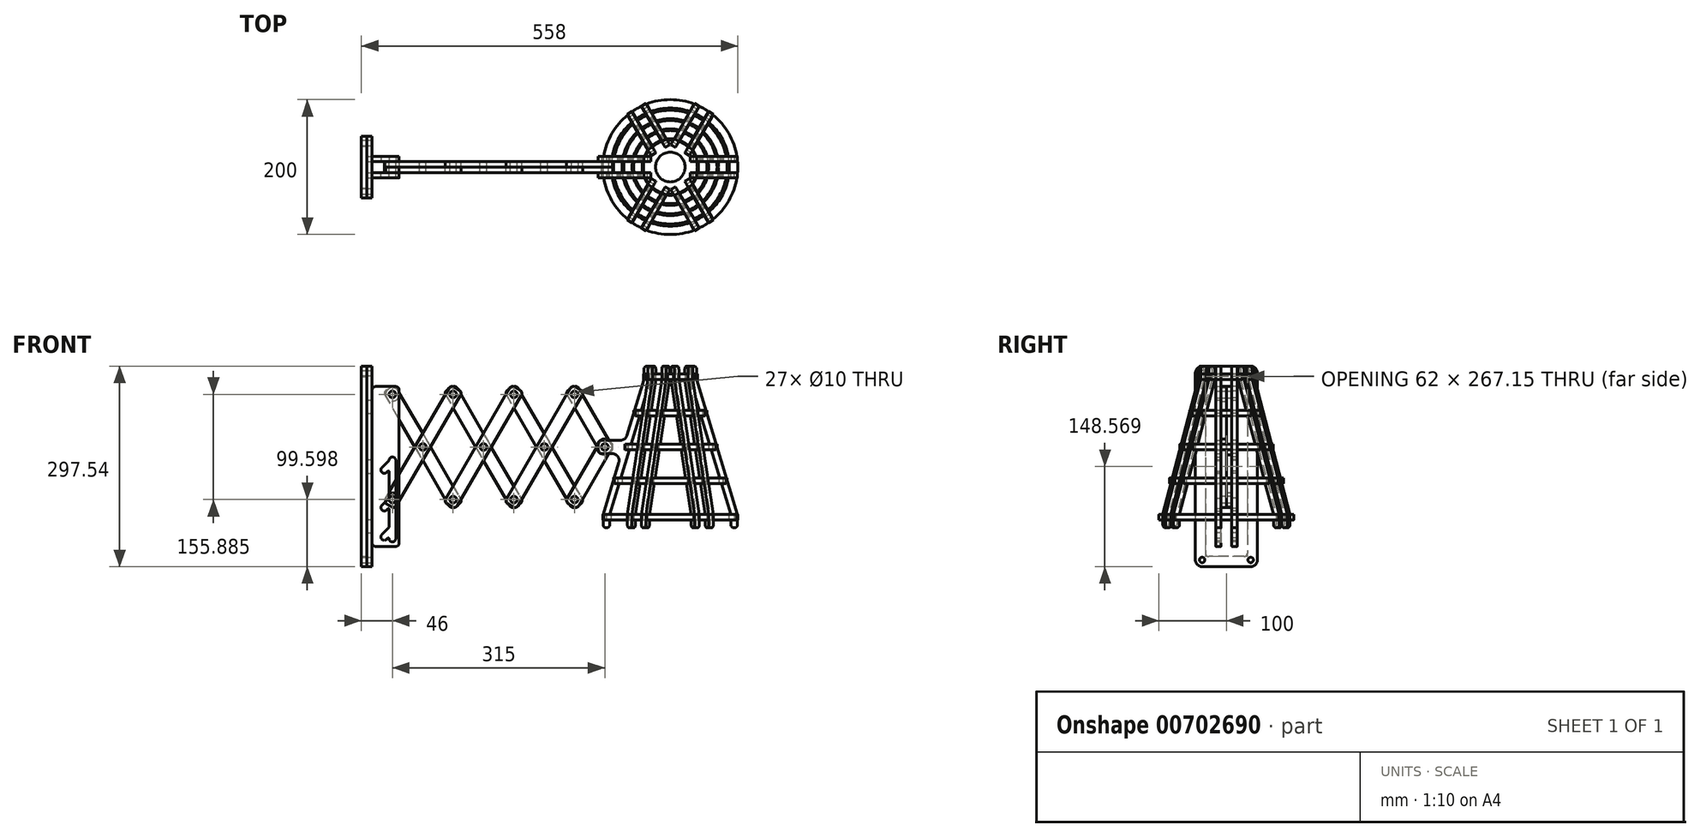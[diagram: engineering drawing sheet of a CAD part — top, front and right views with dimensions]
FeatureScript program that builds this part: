
annotation { "Feature Type Name" : "Feature", "Feature Type Description" : "" }
export const myFeature = defineFeature(function(context is Context, id is Id, definition is map)
    precondition{}
    {
        {
            var Q0;
            Q0=qCreatedBy(makeId("Front.planeOp"),FACE);
            var sketch = newSketch(context, id + "F0", { "sketchPlane" : qUnion([Q0])});
            skLineSegment(sketch, "E0.bottom", {"start": v(54.33, 84.1) * mm, "end": v(45.67, 89.1) * mm});
            skLineSegment(sketch, "E0.top", {"start": v(-45.67, -89.1) * mm, "end": v(-54.33, -84.1) * mm});
            skLineSegment(sketch, "E0.left", {"start": v(56.16, 77.27) * mm, "end": v(-38.84, -87.27) * mm});
            skLineSegment(sketch, "E0.right", {"start": v(38.84, 87.27) * mm, "end": v(-56.16, -77.27) * mm});
            skPoint(sketch, "E0.middle", {"position": v(0, 0) * mm});
            skLineSegment(sketch, "E1", {"start": v(0, 185.82) * mm, "end": v(0, -203.94) * mm, "construction": true});
            skLineSegment(sketch, "E2", {"start": v(-279.88, 0) * mm, "end": v(337.24, 0) * mm, "construction": true});
            skCircle(sketch, "E3", {"center": v(0, 0) * mm, "radius": 5 * mm});
            skCircle(sketch, "E4", {"center": v(45, 77.94) * mm, "radius": 5 * mm});
            skCircle(sketch, "E5.MirrorC", {"center": v(-45, -77.94) * mm, "radius": 5 * mm});
            skPoint(sketch, "E6.visualSharp", {"position": v(41.34, 91.6) * mm});
            skArc(sketch, "E6.filletArc", {"start": v(45.67, 89.1) * mm, "mid": v(41.88, 89.6) * mm, "end": v(38.84, 87.27) * mm});
            skPoint(sketch, "E7.visualSharp", {"position": v(58.66, 81.6) * mm});
            skArc(sketch, "E7.filletArc", {"start": v(56.16, 77.27) * mm, "mid": v(56.66, 81.07) * mm, "end": v(54.33, 84.1) * mm});
            skPoint(sketch, "E8.visualSharp", {"position": v(-41.34, -91.6) * mm});
            skArc(sketch, "E8.filletArc", {"start": v(-45.67, -89.1) * mm, "mid": v(-41.88, -89.6) * mm, "end": v(-38.84, -87.27) * mm});
            skPoint(sketch, "E9.visualSharp", {"position": v(-58.66, -81.6) * mm});
            skArc(sketch, "E9.filletArc", {"start": v(-56.16, -77.27) * mm, "mid": v(-56.66, -81.07) * mm, "end": v(-54.33, -84.1) * mm});
            skSolve(sketch);
        }
        {
            var Q0;
            Q0=makeQuery(id+"F0.imprint","IMPRINT",FACE,{"disambiguationData":[TD([[makeQuery(id+"F0.imprint","IMPRINT",EDGE,{"derivedFrom":sQuery(id+"F0.wireOp",EDGE,"E0.bottom")}),1.0]])]});
            var Q1;
            Q1=makeQuery(id+"F0.imprint","IMPRINT",FACE,{"disambiguationData":[TD([[makeQuery(id+"F0.imprint","IMPRINT",EDGE,{"derivedFrom":sQuery(id+"F0.wireOp",EDGE,"E3")}),-1.0]])]});
            var Q2;
            Q2=makeQuery(id+"F0.imprint","IMPRINT",FACE,{"disambiguationData":[TD([[makeQuery(id+"F0.imprint","IMPRINT",EDGE,{"derivedFrom":sQuery(id+"F0.wireOp",EDGE,"E0.top")}),-1.0]])]});
            var Q3;
            Q3=sQuery(id+"F0.wireOp",EDGE,"E0.right");
            var Q4;
            Q4=sQuery(id+"F0.wireOp",EDGE,"E0.left");
            extrude(context, id + "F1", {"entities" : qUnion([Q0, Q1, Q2]), "surfaceEntities" : qUnion([Q3, Q4]), "depth" : 8 * mm, "offsetDistance" : 25 * mm});
        }
        {
            var Q0;
            Q0=makeQuery(id+"F1.opExtrude","SWEPT_BODY",BODY,{"disambiguationData":[OSD([sQuery(id+"F0.wireOp",EDGE,"E0.bottom"),sQuery(id+"F0.wireOp",EDGE,"E0.top"),sQuery(id+"F0.wireOp",EDGE,"E0.left"),sQuery(id+"F0.wireOp",EDGE,"E0.right"),sQuery(id+"F0.wireOp",EDGE,"E3"),sQuery(id+"F0.wireOp",EDGE,"E4"),sQuery(id+"F0.wireOp",EDGE,"E5.MirrorC"),sQuery(id+"F0.wireOp",EDGE,"E6.filletArc"),sQuery(id+"F0.wireOp",EDGE,"E7.filletArc"),sQuery(id+"F0.wireOp",EDGE,"E8.filletArc"),sQuery(id+"F0.wireOp",EDGE,"E9.filletArc")])]});
            var Q1;
            Q1=qCreatedBy(makeId("Right.planeOp"),FACE);
            mirror(context, id + "F2", {"entities" : qUnion([Q0]), "mirrorPlane" : qUnion([Q1])});
        }
        {
            var Q0;
            Q0=makeQuery(id+"F2.opPattern","COPY",BODY,{"derivedFrom":makeQuery(id+"F1.opExtrude","SWEPT_BODY",BODY,{"disambiguationData":[OSD([sQuery(id+"F0.wireOp",EDGE,"E0.bottom"),sQuery(id+"F0.wireOp",EDGE,"E0.top"),sQuery(id+"F0.wireOp",EDGE,"E0.left"),sQuery(id+"F0.wireOp",EDGE,"E0.right"),sQuery(id+"F0.wireOp",EDGE,"E3"),sQuery(id+"F0.wireOp",EDGE,"E4"),sQuery(id+"F0.wireOp",EDGE,"E5.MirrorC"),sQuery(id+"F0.wireOp",EDGE,"E6.filletArc"),sQuery(id+"F0.wireOp",EDGE,"E7.filletArc"),sQuery(id+"F0.wireOp",EDGE,"E8.filletArc"),sQuery(id+"F0.wireOp",EDGE,"E9.filletArc")])]}),"instanceName":"1"});
            transform(context, id + "F3", {"entities" : qUnion([Q0]), "transformType" : TransformType.TRANSLATION_3D, "dx" : 0 * mm, "dy" : 8 * mm, "dz" : 0 * mm, "makeCopy" : false});
        }
        {
            var Q0;
            Q0=makeQuery(id+"F1.opExtrude","SWEPT_BODY",BODY,{"disambiguationData":[OSD([sQuery(id+"F0.wireOp",EDGE,"E0.bottom"),sQuery(id+"F0.wireOp",EDGE,"E0.top"),sQuery(id+"F0.wireOp",EDGE,"E0.left"),sQuery(id+"F0.wireOp",EDGE,"E0.right"),sQuery(id+"F0.wireOp",EDGE,"E3"),sQuery(id+"F0.wireOp",EDGE,"E4"),sQuery(id+"F0.wireOp",EDGE,"E5.MirrorC"),sQuery(id+"F0.wireOp",EDGE,"E6.filletArc"),sQuery(id+"F0.wireOp",EDGE,"E7.filletArc"),sQuery(id+"F0.wireOp",EDGE,"E8.filletArc"),sQuery(id+"F0.wireOp",EDGE,"E9.filletArc")])]});
            transform(context, id + "F4", {"entities" : qUnion([Q0]), "transformType" : TransformType.TRANSLATION_3D, "dx" : 90 * mm, "dy" : 0 * mm, "dz" : 0 * mm, "makeCopy" : true});
        }
        {
            var Q0;
            Q0=makeQuery(id+"F2.opPattern","COPY",BODY,{"derivedFrom":makeQuery(id+"F1.opExtrude","SWEPT_BODY",BODY,{"disambiguationData":[OSD([sQuery(id+"F0.wireOp",EDGE,"E0.bottom"),sQuery(id+"F0.wireOp",EDGE,"E0.top"),sQuery(id+"F0.wireOp",EDGE,"E0.left"),sQuery(id+"F0.wireOp",EDGE,"E0.right"),sQuery(id+"F0.wireOp",EDGE,"E3"),sQuery(id+"F0.wireOp",EDGE,"E4"),sQuery(id+"F0.wireOp",EDGE,"E5.MirrorC"),sQuery(id+"F0.wireOp",EDGE,"E6.filletArc"),sQuery(id+"F0.wireOp",EDGE,"E7.filletArc"),sQuery(id+"F0.wireOp",EDGE,"E8.filletArc"),sQuery(id+"F0.wireOp",EDGE,"E9.filletArc")])]}),"instanceName":"1"});
            transform(context, id + "F5", {"entities" : qUnion([Q0]), "transformType" : TransformType.TRANSLATION_3D, "dx" : -90 * mm, "dy" : 0 * mm, "dz" : 0 * mm, "makeCopy" : true});
        }
        {
            var Q0;
            Q0=makeQuery(id+"F1.opExtrude","SWEPT_BODY",BODY,{"disambiguationData":[OSD([sQuery(id+"F0.wireOp",EDGE,"E0.bottom"),sQuery(id+"F0.wireOp",EDGE,"E0.top"),sQuery(id+"F0.wireOp",EDGE,"E0.left"),sQuery(id+"F0.wireOp",EDGE,"E0.right"),sQuery(id+"F0.wireOp",EDGE,"E3"),sQuery(id+"F0.wireOp",EDGE,"E4"),sQuery(id+"F0.wireOp",EDGE,"E5.MirrorC"),sQuery(id+"F0.wireOp",EDGE,"E6.filletArc"),sQuery(id+"F0.wireOp",EDGE,"E7.filletArc"),sQuery(id+"F0.wireOp",EDGE,"E8.filletArc"),sQuery(id+"F0.wireOp",EDGE,"E9.filletArc")])]});
            transform(context, id + "F6", {"entities" : qUnion([Q0]), "transformType" : TransformType.TRANSLATION_3D, "dx" : -90 * mm, "dy" : 0 * mm, "dz" : 0 * mm, "makeCopy" : true});
        }
        {
            var Q0;
            Q0=makeQuery(id+"F2.opPattern","COPY",BODY,{"derivedFrom":makeQuery(id+"F1.opExtrude","SWEPT_BODY",BODY,{"disambiguationData":[OSD([sQuery(id+"F0.wireOp",EDGE,"E0.bottom"),sQuery(id+"F0.wireOp",EDGE,"E0.top"),sQuery(id+"F0.wireOp",EDGE,"E0.left"),sQuery(id+"F0.wireOp",EDGE,"E0.right"),sQuery(id+"F0.wireOp",EDGE,"E3"),sQuery(id+"F0.wireOp",EDGE,"E4"),sQuery(id+"F0.wireOp",EDGE,"E5.MirrorC"),sQuery(id+"F0.wireOp",EDGE,"E6.filletArc"),sQuery(id+"F0.wireOp",EDGE,"E7.filletArc"),sQuery(id+"F0.wireOp",EDGE,"E8.filletArc"),sQuery(id+"F0.wireOp",EDGE,"E9.filletArc")])]}),"instanceName":"1"});
            transform(context, id + "F7", {"entities" : qUnion([Q0]), "transformType" : TransformType.TRANSLATION_3D, "dx" : 90 * mm, "dy" : 0 * mm, "dz" : 0 * mm, "makeCopy" : true});
        }
        {
            var Q0;
            Q0=makeQuery(id+"F7.opPattern","COPY",FACE,{"derivedFrom":makeQuery(id+"F2.opPattern","COPY",FACE,{"derivedFrom":makeQuery(id+"F1.opExtrude","CAP_FACE",FACE,{"disambiguationData":[OSD([sQuery(id+"F0.wireOp",EDGE,"E0.bottom"),sQuery(id+"F0.wireOp",EDGE,"E0.top"),sQuery(id+"F0.wireOp",EDGE,"E0.left"),sQuery(id+"F0.wireOp",EDGE,"E0.right"),sQuery(id+"F0.wireOp",EDGE,"E3"),sQuery(id+"F0.wireOp",EDGE,"E4"),sQuery(id+"F0.wireOp",EDGE,"E5.MirrorC"),sQuery(id+"F0.wireOp",EDGE,"E6.filletArc"),sQuery(id+"F0.wireOp",EDGE,"E7.filletArc"),sQuery(id+"F0.wireOp",EDGE,"E8.filletArc"),sQuery(id+"F0.wireOp",EDGE,"E9.filletArc")])],"isStart":true}),"instanceName":"1"}),"instanceName":"1"});
            var sketch = newSketch(context, id + "F8", { "sketchPlane" : qUnion([Q0])});
            skCircle(sketch, "E10.0", {"center": v(135, 77.94) * mm, "radius": 5 * mm});
            skLineSegment(sketch, "E11", {"start": v(130, 89.6) * mm, "end": v(160, 89.6) * mm, "construction": true});
            skPoint(sketch, "E11.startSnap0", {"position": v(41.88, 89.6) * mm});
            skLineSegment(sketch, "E12", {"start": v(22.72, 0) * mm, "end": v(188.2, 0) * mm, "construction": true});
            skLineSegment(sketch, "E13", {"start": v(130, 89.6) * mm, "end": v(160, 89.6) * mm});
            skLineSegment(sketch, "E14", {"start": v(135, 121.8) * mm, "end": v(135, -172.81) * mm, "construction": true});
            skArc(sketch, "E15.0", {"start": v(140, -20) * mm, "mid": v(135, -15) * mm, "end": v(130, -20) * mm});
            skLineSegment(sketch, "E16", {"start": v(95.12, -77.94) * mm, "end": v(188.2, -77.94) * mm, "construction": true});
            skArc(sketch, "E17.MirrorC", {"start": v(140, -135.88) * mm, "mid": v(135, -140.88) * mm, "end": v(130, -135.88) * mm});
            skLineSegment(sketch, "E18", {"start": v(130, -147.54) * mm, "end": v(160, -147.54) * mm});
            skLineSegment(sketch, "E19", {"start": v(125, 84.6) * mm, "end": v(125, -142.54) * mm});
            skLineSegment(sketch, "E20", {"start": v(165, 84.6) * mm, "end": v(165, 69.6) * mm});
            skLineSegment(sketch, "E21", {"start": v(130, -135.88) * mm, "end": v(130, -20) * mm});
            skLineSegment(sketch, "E22.MirrorCS", {"start": v(140, -119.33) * mm, "end": v(140, -92.37) * mm});
            skPoint(sketch, "E23.newPointB", {"position": v(24.22, 89.6) * mm});
            skArc(sketch, "E23.filletArc", {"start": v(130, 89.6) * mm, "mid": v(126.46, 88.14) * mm, "end": v(125, 84.6) * mm});
            skPoint(sketch, "E24.newPointA", {"position": v(188.2, 89.6) * mm});
            skArc(sketch, "E24.filletArc", {"start": v(165, 84.6) * mm, "mid": v(163.54, 88.14) * mm, "end": v(160, 89.6) * mm});
            skPoint(sketch, "E25.visualSharp", {"position": v(125, -147.54) * mm});
            skArc(sketch, "E25.filletArc", {"start": v(125, -142.54) * mm, "mid": v(126.46, -146.08) * mm, "end": v(130, -147.54) * mm});
            skPoint(sketch, "E26.visualSharp", {"position": v(165, -147.54) * mm});
            skArc(sketch, "E26.filletArc", {"start": v(160, -147.54) * mm, "mid": v(163.54, -146.08) * mm, "end": v(165, -142.54) * mm});
            skLineSegment(sketch, "E27", {"start": v(165, 69.6) * mm, "end": v(173, 69.6) * mm});
            skLineSegment(sketch, "E28", {"start": v(173, 69.6) * mm, "end": v(173, 49.6) * mm});
            skLineSegment(sketch, "E29", {"start": v(173, 49.6) * mm, "end": v(165, 49.6) * mm});
            skLineSegment(sketch, "E30", {"start": v(165, -107.54) * mm, "end": v(173, -107.54) * mm});
            skLineSegment(sketch, "E31", {"start": v(173, -107.54) * mm, "end": v(173, -127.54) * mm});
            skLineSegment(sketch, "E32", {"start": v(173, -127.54) * mm, "end": v(165, -127.54) * mm});
            skLineSegment(sketch, "E33.trimOffspring", {"start": v(165, -127.54) * mm, "end": v(165, -142.54) * mm});
            skLineSegment(sketch, "E34.trimOffspring", {"start": v(165, 49.6) * mm, "end": v(165, -18.97) * mm});
            skLineSegment(sketch, "E35", {"start": v(165, -18.97) * mm, "end": v(173, -18.97) * mm});
            skLineSegment(sketch, "E36", {"start": v(173, -18.97) * mm, "end": v(173, -38.97) * mm});
            skLineSegment(sketch, "E37", {"start": v(173, -38.97) * mm, "end": v(165, -38.97) * mm});
            skLineSegment(sketch, "E38.trimOffspring", {"start": v(165, -38.97) * mm, "end": v(165, -107.54) * mm});
            skPoint(sketch, "E39.orphan", {"position": v(165, -28.97) * mm});
            skArc(sketch, "E40", {"start": v(143.5, -93.46) * mm, "mid": v(150.57, -93.46) * mm, "end": v(150.57, -86.4) * mm});
            skLineSegment(sketch, "E41", {"start": v(150.57, -86.4) * mm, "end": v(140, -75.82) * mm});
            skLineSegment(sketch, "E42.MirrorCS", {"start": v(143.5, -93.46) * mm, "end": v(141.7, -91.67) * mm});
            skArc(sketch, "E43.filletArc", {"start": v(141.7, -91.67) * mm, "mid": v(140.62, -91.45) * mm, "end": v(140, -92.37) * mm});
            skArc(sketch, "E44", {"start": v(143.5, -136.97) * mm, "mid": v(150.57, -136.97) * mm, "end": v(150.57, -129.9) * mm});
            skLineSegment(sketch, "E45", {"start": v(150.57, -129.9) * mm, "end": v(140, -119.33) * mm});
            skLineSegment(sketch, "E46.MirrorCS", {"start": v(143.5, -136.97) * mm, "end": v(141.7, -135.18) * mm});
            skArc(sketch, "E47.filletArc", {"start": v(141.7, -135.18) * mm, "mid": v(140.62, -134.96) * mm, "end": v(140, -135.88) * mm});
            skArc(sketch, "E48", {"start": v(143.5, -37.65) * mm, "mid": v(150.57, -37.65) * mm, "end": v(150.57, -30.57) * mm});
            skLineSegment(sketch, "E49", {"start": v(150.57, -30.57) * mm, "end": v(140, -20) * mm});
            skLineSegment(sketch, "E50.MirrorCS", {"start": v(143.5, -37.65) * mm, "end": v(141.7, -35.85) * mm});
            skArc(sketch, "E51.filletArc", {"start": v(141.7, -35.85) * mm, "mid": v(140.62, -35.63) * mm, "end": v(140, -36.56) * mm});
            skLineSegment(sketch, "E52.trimOffspring", {"start": v(140, -75.82) * mm, "end": v(140, -36.56) * mm});
            skSolve(sketch);
        }
        {
            var Q0;
            Q0=qSketchRegion(id+"F8",true);
            extrude(context, id + "F9", {"entities" : qUnion([Q0]), "depth" : 8 * mm, "offsetDistance" : 25 * mm});
        }
        {
            var Q0;
            Q0=makeQuery(id+"F9.opExtrude","SWEPT_BODY",BODY,{"disambiguationData":[OSD([sQuery(id+"F8.wireOp",EDGE,"E10.0"),sQuery(id+"F8.wireOp",EDGE,"E13"),sQuery(id+"F8.wireOp",EDGE,"E15.0"),sQuery(id+"F8.wireOp",EDGE,"E17.MirrorC"),sQuery(id+"F8.wireOp",EDGE,"E18"),sQuery(id+"F8.wireOp",EDGE,"E19"),sQuery(id+"F8.wireOp",EDGE,"E20"),sQuery(id+"F8.wireOp",EDGE,"E21"),sQuery(id+"F8.wireOp",EDGE,"E22.MirrorCS"),sQuery(id+"F8.wireOp",EDGE,"E23.filletArc"),sQuery(id+"F8.wireOp",EDGE,"E24.filletArc"),sQuery(id+"F8.wireOp",EDGE,"E25.filletArc"),sQuery(id+"F8.wireOp",EDGE,"E26.filletArc")])]});
            var Q1;
            Q1=qCreatedBy(makeId("Front.planeOp"),FACE);
            mirror(context, id + "F10", {"entities" : qUnion([Q0]), "mirrorPlane" : qUnion([Q1])});
        }
        {
            var Q0;
            Q0=makeQuery(id+"F9.opExtrude","SWEPT_FACE",FACE,{"disambiguationData":[OSD([sQuery(id+"F8.wireOp",EDGE,"E34.trimOffspring")])]});
            var sketch = newSketch(context, id + "F11", { "sketchPlane" : qUnion([Q0])});
            skPoint(sketch, "E53.middle", {"position": v(0, 0) * mm});
            skLineSegment(sketch, "E54.0.0", {"start": v(-8, 49.6) * mm, "end": v(-8, 69.6) * mm});
            skLineSegment(sketch, "E54.0.1", {"start": v(-8, 69.6) * mm, "end": v(-16, 69.6) * mm});
            skLineSegment(sketch, "E54.0.2", {"start": v(-16, 69.6) * mm, "end": v(-16, 49.6) * mm});
            skLineSegment(sketch, "E54.0.3", {"start": v(-16, 49.6) * mm, "end": v(-8, 49.6) * mm});
            skLineSegment(sketch, "E55.0.0", {"start": v(8, 69.6) * mm, "end": v(8, 49.6) * mm});
            skLineSegment(sketch, "E55.0.1", {"start": v(8, 49.6) * mm, "end": v(16, 49.6) * mm});
            skLineSegment(sketch, "E55.0.2", {"start": v(16, 49.6) * mm, "end": v(16, 69.6) * mm});
            skLineSegment(sketch, "E55.0.3", {"start": v(16, 69.6) * mm, "end": v(8, 69.6) * mm});
            skLineSegment(sketch, "E56.0.0", {"start": v(-8, -38.97) * mm, "end": v(-8, -18.97) * mm});
            skLineSegment(sketch, "E56.0.1", {"start": v(-8, -18.97) * mm, "end": v(-16, -18.97) * mm});
            skLineSegment(sketch, "E56.0.2", {"start": v(-16, -18.97) * mm, "end": v(-16, -38.97) * mm});
            skLineSegment(sketch, "E56.0.3", {"start": v(-16, -38.97) * mm, "end": v(-8, -38.97) * mm});
            skLineSegment(sketch, "E57.0.0", {"start": v(8, -18.97) * mm, "end": v(8, -38.97) * mm});
            skLineSegment(sketch, "E57.0.1", {"start": v(8, -38.97) * mm, "end": v(16, -38.97) * mm});
            skLineSegment(sketch, "E57.0.2", {"start": v(16, -38.97) * mm, "end": v(16, -18.97) * mm});
            skLineSegment(sketch, "E57.0.3", {"start": v(16, -18.97) * mm, "end": v(8, -18.97) * mm});
            skLineSegment(sketch, "E58.0.0", {"start": v(-8, -127.54) * mm, "end": v(-8, -107.54) * mm});
            skLineSegment(sketch, "E58.0.1", {"start": v(-8, -107.54) * mm, "end": v(-16, -107.54) * mm});
            skLineSegment(sketch, "E58.0.2", {"start": v(-16, -107.54) * mm, "end": v(-16, -127.54) * mm});
            skLineSegment(sketch, "E58.0.3", {"start": v(-16, -127.54) * mm, "end": v(-8, -127.54) * mm});
            skLineSegment(sketch, "E59.0.0", {"start": v(8, -107.54) * mm, "end": v(8, -127.54) * mm});
            skLineSegment(sketch, "E59.0.1", {"start": v(8, -127.54) * mm, "end": v(16, -127.54) * mm});
            skLineSegment(sketch, "E59.0.2", {"start": v(16, -127.54) * mm, "end": v(16, -107.54) * mm});
            skLineSegment(sketch, "E59.0.3", {"start": v(16, -107.54) * mm, "end": v(8, -107.54) * mm});
            skLineSegment(sketch, "E60", {"start": v(46, 109.6) * mm, "end": v(46, -167.54) * mm});
            skLineSegment(sketch, "E61", {"start": v(-36, 119.6) * mm, "end": v(36, 119.6) * mm});
            skLineSegment(sketch, "E62", {"start": v(-36, -177.54) * mm, "end": v(36, -177.54) * mm});
            skLineSegment(sketch, "E63.MirrorCS", {"start": v(-46, 109.6) * mm, "end": v(-46, -167.54) * mm});
            skPoint(sketch, "E64.visualSharp", {"position": v(-46, 119.6) * mm});
            skArc(sketch, "E64.filletArc", {"start": v(-36, 119.6) * mm, "mid": v(-43.07, 116.67) * mm, "end": v(-46, 109.6) * mm});
            skPoint(sketch, "E65.visualSharp", {"position": v(46, 119.6) * mm});
            skArc(sketch, "E65.filletArc", {"start": v(46, 109.6) * mm, "mid": v(43.07, 116.67) * mm, "end": v(36, 119.6) * mm});
            skPoint(sketch, "E66.visualSharp", {"position": v(-46, -177.54) * mm});
            skArc(sketch, "E66.filletArc", {"start": v(-46, -167.54) * mm, "mid": v(-43.07, -174.62) * mm, "end": v(-36, -177.54) * mm});
            skPoint(sketch, "E67.visualSharp", {"position": v(46, -177.54) * mm});
            skArc(sketch, "E67.filletArc", {"start": v(36, -177.54) * mm, "mid": v(43.07, -174.62) * mm, "end": v(46, -167.54) * mm});
            skCircle(sketch, "E68", {"center": v(-36, 109.6) * mm, "radius": 4 * mm});
            skCircle(sketch, "E69", {"center": v(36, 109.6) * mm, "radius": 4 * mm});
            skCircle(sketch, "E70", {"center": v(-36, -167.54) * mm, "radius": 4 * mm});
            skCircle(sketch, "E71", {"center": v(36, -167.54) * mm, "radius": 4 * mm});
            skSolve(sketch);
        }
        {
            var Q0;
            Q0=qSketchRegion(id+"F11",true);
            extrude(context, id + "F12", {"entities" : qUnion([Q0]), "depth" : 8 * mm, "offsetDistance" : 25 * mm});
        }
        {
            var Q0;
            Q0=makeQuery(id+"F12.opExtrude","CAP_FACE",FACE,{"disambiguationData":[OSD([sQuery(id+"F11.wireOp",EDGE,"E54.0.0"),sQuery(id+"F11.wireOp",EDGE,"E54.0.1"),sQuery(id+"F11.wireOp",EDGE,"E54.0.2"),sQuery(id+"F11.wireOp",EDGE,"E54.0.3"),sQuery(id+"F11.wireOp",EDGE,"E55.0.0"),sQuery(id+"F11.wireOp",EDGE,"E55.0.1"),sQuery(id+"F11.wireOp",EDGE,"E55.0.2"),sQuery(id+"F11.wireOp",EDGE,"E55.0.3"),sQuery(id+"F11.wireOp",EDGE,"E56.0.0"),sQuery(id+"F11.wireOp",EDGE,"E56.0.1"),sQuery(id+"F11.wireOp",EDGE,"E56.0.2"),sQuery(id+"F11.wireOp",EDGE,"E56.0.3"),sQuery(id+"F11.wireOp",EDGE,"E57.0.0"),sQuery(id+"F11.wireOp",EDGE,"E57.0.1"),sQuery(id+"F11.wireOp",EDGE,"E57.0.2"),sQuery(id+"F11.wireOp",EDGE,"E57.0.3"),sQuery(id+"F11.wireOp",EDGE,"E58.0.0"),sQuery(id+"F11.wireOp",EDGE,"E58.0.1"),sQuery(id+"F11.wireOp",EDGE,"E58.0.2"),sQuery(id+"F11.wireOp",EDGE,"E58.0.3"),sQuery(id+"F11.wireOp",EDGE,"E59.0.0"),sQuery(id+"F11.wireOp",EDGE,"E59.0.1"),sQuery(id+"F11.wireOp",EDGE,"E59.0.2"),sQuery(id+"F11.wireOp",EDGE,"E59.0.3"),sQuery(id+"F11.wireOp",EDGE,"E60"),sQuery(id+"F11.wireOp",EDGE,"E61"),sQuery(id+"F11.wireOp",EDGE,"E62"),sQuery(id+"F11.wireOp",EDGE,"E63.MirrorCS"),sQuery(id+"F11.wireOp",EDGE,"E64.filletArc"),sQuery(id+"F11.wireOp",EDGE,"E65.filletArc"),sQuery(id+"F11.wireOp",EDGE,"E66.filletArc"),sQuery(id+"F11.wireOp",EDGE,"E67.filletArc"),sQuery(id+"F11.wireOp",EDGE,"E68"),sQuery(id+"F11.wireOp",EDGE,"E69"),sQuery(id+"F11.wireOp",EDGE,"E70"),sQuery(id+"F11.wireOp",EDGE,"E71")])],"isStart":false});
            var sketch = newSketch(context, id + "F13", { "sketchPlane" : qUnion([Q0])});
            skArc(sketch, "E72.0.0", {"start": v(-36, 119.6) * mm, "mid": v(-43.07, 116.67) * mm, "end": v(-46, 109.6) * mm});
            skLineSegment(sketch, "E72.0.1", {"start": v(-46, 109.6) * mm, "end": v(-46, -167.54) * mm});
            skArc(sketch, "E72.0.2", {"start": v(-46, -167.54) * mm, "mid": v(-43.07, -174.62) * mm, "end": v(-36, -177.54) * mm});
            skLineSegment(sketch, "E72.0.3", {"start": v(-36, -177.54) * mm, "end": v(36, -177.54) * mm});
            skArc(sketch, "E72.0.4", {"start": v(36, -177.54) * mm, "mid": v(43.07, -174.62) * mm, "end": v(46, -167.54) * mm});
            skLineSegment(sketch, "E72.0.5", {"start": v(46, -167.54) * mm, "end": v(46, 109.6) * mm});
            skArc(sketch, "E72.0.6", {"start": v(46, 109.6) * mm, "mid": v(43.07, 116.67) * mm, "end": v(36, 119.6) * mm});
            skLineSegment(sketch, "E72.0.7", {"start": v(36, 119.6) * mm, "end": v(-36, 119.6) * mm});
            skCircle(sketch, "E73.0", {"center": v(-36, 109.6) * mm, "radius": 4 * mm});
            skCircle(sketch, "E74.0", {"center": v(36, 109.6) * mm, "radius": 4 * mm});
            skCircle(sketch, "E75.0", {"center": v(-36, -167.54) * mm, "radius": 4 * mm});
            skCircle(sketch, "E76.0", {"center": v(36, -167.54) * mm, "radius": 4 * mm});
            skLineSegment(sketch, "E77.bottom", {"start": v(-26, 104.6) * mm, "end": v(26, 104.6) * mm});
            skLineSegment(sketch, "E77.top", {"start": v(-26, -162.54) * mm, "end": v(26, -162.54) * mm});
            skLineSegment(sketch, "E77.left", {"start": v(-31, 99.6) * mm, "end": v(-31, -157.54) * mm});
            skLineSegment(sketch, "E77.right", {"start": v(31, 99.6) * mm, "end": v(31, -157.54) * mm});
            skPoint(sketch, "E78.visualSharp", {"position": v(-31, 104.6) * mm});
            skArc(sketch, "E78.filletArc", {"start": v(-26, 104.6) * mm, "mid": v(-29.54, 103.14) * mm, "end": v(-31, 99.6) * mm});
            skPoint(sketch, "E79.visualSharp", {"position": v(31, 104.6) * mm});
            skArc(sketch, "E79.filletArc", {"start": v(31, 99.6) * mm, "mid": v(29.54, 103.14) * mm, "end": v(26, 104.6) * mm});
            skPoint(sketch, "E80.visualSharp", {"position": v(-31, -162.54) * mm});
            skArc(sketch, "E80.filletArc", {"start": v(-31, -157.54) * mm, "mid": v(-29.54, -161.08) * mm, "end": v(-26, -162.54) * mm});
            skPoint(sketch, "E81.visualSharp", {"position": v(31, -162.54) * mm});
            skArc(sketch, "E81.filletArc", {"start": v(26, -162.54) * mm, "mid": v(29.54, -161.08) * mm, "end": v(31, -157.54) * mm});
            skSolve(sketch);
        }
        {
            var Q0;
            Q0=qSketchRegion(id+"F13",true);
            extrude(context, id + "F14", {"entities" : qUnion([Q0]), "depth" : 8 * mm, "offsetDistance" : 25 * mm});
        }
        {
            var Q0;
            Q0=makeQuery(id+"F6.opPattern","COPY",FACE,{"derivedFrom":makeQuery(id+"F1.opExtrude","CAP_FACE",FACE,{"disambiguationData":[OSD([sQuery(id+"F0.wireOp",EDGE,"E0.bottom"),sQuery(id+"F0.wireOp",EDGE,"E0.top"),sQuery(id+"F0.wireOp",EDGE,"E0.left"),sQuery(id+"F0.wireOp",EDGE,"E0.right"),sQuery(id+"F0.wireOp",EDGE,"E3"),sQuery(id+"F0.wireOp",EDGE,"E4"),sQuery(id+"F0.wireOp",EDGE,"E5.MirrorC"),sQuery(id+"F0.wireOp",EDGE,"E6.filletArc"),sQuery(id+"F0.wireOp",EDGE,"E7.filletArc"),sQuery(id+"F0.wireOp",EDGE,"E8.filletArc"),sQuery(id+"F0.wireOp",EDGE,"E9.filletArc")])],"isStart":true}),"instanceName":"1"});
            var sketch = newSketch(context, id + "F15", { "sketchPlane" : qUnion([Q0])});
            skCircle(sketch, "E82.0", {"center": v(135, -77.94) * mm, "radius": 5 * mm});
            skCircle(sketch, "E83", {"center": v(135, -77.94) * mm, "radius": 10 * mm});
            skSolve(sketch);
        }
        {
            var Q0;
            Q0=qSketchRegion(id+"F15",true);
            extrude(context, id + "F16", {"entities" : qUnion([Q0]), "depth" : 8 * mm, "offsetDistance" : 25 * mm});
        }
        {
            var Q0;
            Q0=makeQuery(id+"F5.opPattern","COPY",FACE,{"derivedFrom":makeQuery(id+"F2.opPattern","COPY",FACE,{"derivedFrom":makeQuery(id+"F1.opExtrude","CAP_FACE",FACE,{"disambiguationData":[OSD([sQuery(id+"F0.wireOp",EDGE,"E0.bottom"),sQuery(id+"F0.wireOp",EDGE,"E0.top"),sQuery(id+"F0.wireOp",EDGE,"E0.left"),sQuery(id+"F0.wireOp",EDGE,"E0.right"),sQuery(id+"F0.wireOp",EDGE,"E3"),sQuery(id+"F0.wireOp",EDGE,"E4"),sQuery(id+"F0.wireOp",EDGE,"E5.MirrorC"),sQuery(id+"F0.wireOp",EDGE,"E6.filletArc"),sQuery(id+"F0.wireOp",EDGE,"E7.filletArc"),sQuery(id+"F0.wireOp",EDGE,"E8.filletArc"),sQuery(id+"F0.wireOp",EDGE,"E9.filletArc")])],"isStart":false}),"instanceName":"1"}),"instanceName":"1"});
            var sketch = newSketch(context, id + "F17", { "sketchPlane" : qUnion([Q0])});
            skCircle(sketch, "E84.0", {"center": v(-135, 77.94) * mm, "radius": 5 * mm});
            skCircle(sketch, "E85", {"center": v(-135, 77.94) * mm, "radius": 10 * mm});
            skSolve(sketch);
        }
        {
            var Q0;
            Q0=qSketchRegion(id+"F17",true);
            extrude(context, id + "F18", {"entities" : qUnion([Q0]), "depth" : 8 * mm, "offsetDistance" : 25 * mm});
        }
        {
            var Q0;
            Q0=makeQuery(id+"F2.opPattern","COPY",FACE,{"derivedFrom":makeQuery(id+"F1.opExtrude","CAP_FACE",FACE,{"disambiguationData":[OSD([sQuery(id+"F0.wireOp",EDGE,"E0.bottom"),sQuery(id+"F0.wireOp",EDGE,"E0.top"),sQuery(id+"F0.wireOp",EDGE,"E0.left"),sQuery(id+"F0.wireOp",EDGE,"E0.right"),sQuery(id+"F0.wireOp",EDGE,"E3"),sQuery(id+"F0.wireOp",EDGE,"E4"),sQuery(id+"F0.wireOp",EDGE,"E5.MirrorC"),sQuery(id+"F0.wireOp",EDGE,"E6.filletArc"),sQuery(id+"F0.wireOp",EDGE,"E7.filletArc"),sQuery(id+"F0.wireOp",EDGE,"E8.filletArc"),sQuery(id+"F0.wireOp",EDGE,"E9.filletArc")])],"isStart":false}),"instanceName":"1"});
            var sketch = newSketch(context, id + "F19", { "sketchPlane" : qUnion([Q0])});
            skLineSegment(sketch, "E86.top", {"start": v(134.33, -89.1) * mm, "end": v(125.67, -84.1) * mm});
            skLineSegment(sketch, "E86.left", {"start": v(191.55, 0) * mm, "end": v(141.16, -87.27) * mm});
            skLineSegment(sketch, "E86.right", {"start": v(173.84, 9.33) * mm, "end": v(123.84, -77.27) * mm});
            skPoint(sketch, "E86.middle", {"position": v(180, 0) * mm});
            skLineSegment(sketch, "E87", {"start": v(180, 185.82) * mm, "end": v(180, -203.94) * mm, "construction": true});
            skLineSegment(sketch, "E88", {"start": v(-99.88, 0) * mm, "end": v(517.24, 0) * mm, "construction": true});
            skCircle(sketch, "E89.MirrorC", {"center": v(135, -77.94) * mm, "radius": 5 * mm});
            skPoint(sketch, "E90.visualSharp", {"position": v(138.66, -91.6) * mm});
            skArc(sketch, "E90.filletArc", {"start": v(134.33, -89.1) * mm, "mid": v(138.12, -89.6) * mm, "end": v(141.16, -87.27) * mm});
            skPoint(sketch, "E91.visualSharp", {"position": v(121.34, -81.6) * mm});
            skArc(sketch, "E91.filletArc", {"start": v(123.84, -77.27) * mm, "mid": v(123.34, -81.07) * mm, "end": v(125.67, -84.1) * mm});
            skLineSegment(sketch, "E92.bottom", {"start": v(189.33, 6.16) * mm, "end": v(180.67, 11.16) * mm});
            skCircle(sketch, "E93", {"center": v(180, 0) * mm, "radius": 5 * mm});
            skArc(sketch, "E94.filletArc", {"start": v(180.67, 11.16) * mm, "mid": v(176.88, 11.66) * mm, "end": v(173.84, 9.33) * mm});
            skArc(sketch, "E95.filletArc", {"start": v(191.16, -0.67) * mm, "mid": v(191.66, 3.12) * mm, "end": v(189.33, 6.16) * mm});
            skSolve(sketch);
        }
        {
            var Q0;
            Q0=qSketchRegion(id+"F19",true);
            extrude(context, id + "F20", {"entities" : qUnion([Q0]), "operationType" : NewBodyOperationType.ADD, "depth" : 8 * mm, "offsetDistance" : 25 * mm});
        }
        {
            var Q0;
            Q0=makeQuery(id+"F4.opPattern","COPY",FACE,{"derivedFrom":makeQuery(id+"F1.opExtrude","CAP_FACE",FACE,{"disambiguationData":[OSD([sQuery(id+"F0.wireOp",EDGE,"E0.bottom"),sQuery(id+"F0.wireOp",EDGE,"E0.top"),sQuery(id+"F0.wireOp",EDGE,"E0.left"),sQuery(id+"F0.wireOp",EDGE,"E0.right"),sQuery(id+"F0.wireOp",EDGE,"E3"),sQuery(id+"F0.wireOp",EDGE,"E4"),sQuery(id+"F0.wireOp",EDGE,"E5.MirrorC"),sQuery(id+"F0.wireOp",EDGE,"E6.filletArc"),sQuery(id+"F0.wireOp",EDGE,"E7.filletArc"),sQuery(id+"F0.wireOp",EDGE,"E8.filletArc"),sQuery(id+"F0.wireOp",EDGE,"E9.filletArc")])],"isStart":true}),"instanceName":"1"});
            var sketch = newSketch(context, id + "F21", { "sketchPlane" : qUnion([Q0])});
            skLineSegment(sketch, "E96.top", {"start": v(-180.67, -11.16) * mm, "end": v(-189.33, -6.16) * mm});
            skLineSegment(sketch, "E96.left", {"start": v(-123.45, 77.94) * mm, "end": v(-173.84, -9.33) * mm});
            skLineSegment(sketch, "E96.right", {"start": v(-141.16, 87.27) * mm, "end": v(-191.16, 0.67) * mm});
            skPoint(sketch, "E96.middle", {"position": v(-135, 77.94) * mm});
            skLineSegment(sketch, "E97", {"start": v(-135, 263.76) * mm, "end": v(-135, -126) * mm, "construction": true});
            skLineSegment(sketch, "E98", {"start": v(-414.88, 77.94) * mm, "end": v(202.24, 77.94) * mm, "construction": true});
            skCircle(sketch, "E99.MirrorC", {"center": v(-180, 0) * mm, "radius": 5 * mm});
            skPoint(sketch, "E100.visualSharp", {"position": v(-176.34, -13.66) * mm});
            skArc(sketch, "E100.filletArc", {"start": v(-180.67, -11.16) * mm, "mid": v(-176.88, -11.66) * mm, "end": v(-173.84, -9.33) * mm});
            skPoint(sketch, "E101.visualSharp", {"position": v(-193.66, -3.66) * mm});
            skArc(sketch, "E101.filletArc", {"start": v(-191.16, 0.67) * mm, "mid": v(-191.66, -3.12) * mm, "end": v(-189.33, -6.16) * mm});
            skLineSegment(sketch, "E102.bottom", {"start": v(-125.67, 84.1) * mm, "end": v(-134.33, 89.1) * mm});
            skCircle(sketch, "E103", {"center": v(-135, 77.94) * mm, "radius": 5 * mm});
            skArc(sketch, "E104.filletArc", {"start": v(-134.33, 89.1) * mm, "mid": v(-138.12, 89.6) * mm, "end": v(-141.16, 87.27) * mm});
            skArc(sketch, "E105.filletArc", {"start": v(-123.84, 77.27) * mm, "mid": v(-123.34, 81.07) * mm, "end": v(-125.67, 84.1) * mm});
            skSolve(sketch);
        }
        {
            var Q0;
            Q0=qSketchRegion(id+"F21",true);
            extrude(context, id + "F22", {"entities" : qUnion([Q0]), "depth" : 8 * mm, "offsetDistance" : 25 * mm});
        }
        {
            var Q0;
            Q0=qCreatedBy(makeId("Top.planeOp"),FACE);
            cPlane(context, id + "F23", {"entities" : qUnion([Q0]), "cplaneType" : CPlaneType.OFFSET, "offset" : 100 * mm, "width" : 150 * mm, "height" : 150 * mm});
        }
        {
            var Q0;
            Q0=qCreatedBy(id+"F23.planeOp",FACE);
            var sketch = newSketch(context, id + "F24", { "sketchPlane" : qUnion([Q0])});
            skLineSegment(sketch, "E106", {"start": v(275, -71.82) * mm, "end": v(275, 43.7) * mm, "construction": true});
            skCircle(sketch, "E107", {"center": v(275, 0) * mm, "radius": 22 * mm});
            skLineSegment(sketch, "E108", {"start": v(166.47, 0) * mm, "end": v(330.06, 0) * mm, "construction": true});
            skLineSegment(sketch, "E109", {"start": v(235.8, -8) * mm, "end": v(240.8, -8) * mm});
            skLineSegment(sketch, "E110", {"start": v(240.8, -8) * mm, "end": v(240.8, -16) * mm});
            skLineSegment(sketch, "E111", {"start": v(240.8, -16) * mm, "end": v(238.34, -16) * mm});
            skLineSegment(sketch, "E112.MirrorCS", {"start": v(235.8, 8) * mm, "end": v(240.8, 8) * mm});
            skLineSegment(sketch, "E113.MirrorCS", {"start": v(240.8, 8) * mm, "end": v(240.8, 16) * mm});
            skLineSegment(sketch, "E114.MirrorCS", {"start": v(240.8, 16) * mm, "end": v(238.34, 16) * mm});
            skLineSegment(sketch, "E115.1.1", {"start": v(250.98, -25.61) * mm, "end": v(244.05, -21.61) * mm});
            skLineSegment(sketch, "E115.1.2", {"start": v(248.48, -29.94) * mm, "end": v(250.98, -25.61) * mm});
            skLineSegment(sketch, "E115.1.3", {"start": v(244.05, -21.61) * mm, "end": v(242.81, -23.75) * mm});
            skLineSegment(sketch, "E115.1.4", {"start": v(271.76, -37.61) * mm, "end": v(270.53, -39.75) * mm});
            skLineSegment(sketch, "E115.1.5", {"start": v(264.83, -33.61) * mm, "end": v(271.76, -37.61) * mm});
            skLineSegment(sketch, "E115.1.6", {"start": v(262.33, -37.94) * mm, "end": v(264.83, -33.61) * mm});
            skArc(sketch, "E116", {"start": v(242.81, 23.75) * mm, "mid": v(240.36, 20) * mm, "end": v(238.34, 16) * mm});
            skArc(sketch, "E117.trimOffspring", {"start": v(262.33, 37.94) * mm, "mid": v(255, 34.64) * mm, "end": v(248.48, 29.94) * mm});
            skArc(sketch, "E118.trimOffspring", {"start": v(238.34, -16) * mm, "mid": v(240.36, -20) * mm, "end": v(242.81, -23.75) * mm});
            skArc(sketch, "E119.trimOffspring", {"start": v(235.8, 8) * mm, "mid": v(235, 0) * mm, "end": v(235.8, -8) * mm});
            skLineSegment(sketch, "E120.0", {"start": v(185, 8) * mm, "end": v(175, 8) * mm, "construction": true});
            skLineSegment(sketch, "E121", {"start": v(185, 8) * mm, "end": v(185, -8) * mm, "construction": true});
            skLineSegment(sketch, "E122", {"start": v(185, -8) * mm, "end": v(175, -8) * mm, "construction": true});
            skLineSegment(sketch, "E123", {"start": v(175, -8) * mm, "end": v(175, 8) * mm, "construction": true});
            skLineSegment(sketch, "E124.2.2.0", {"start": v(285.17, -33.61) * mm, "end": v(278.24, -37.61) * mm});
            skLineSegment(sketch, "E124.5.2.0", {"start": v(287.67, -37.94) * mm, "end": v(285.17, -33.61) * mm});
            skLineSegment(sketch, "E124.8.2.0", {"start": v(278.24, -37.61) * mm, "end": v(279.47, -39.75) * mm});
            skLineSegment(sketch, "E124.11.2.0", {"start": v(305.95, -21.61) * mm, "end": v(307.19, -23.75) * mm});
            skLineSegment(sketch, "E124.14.2.0", {"start": v(299.02, -25.61) * mm, "end": v(305.95, -21.61) * mm});
            skLineSegment(sketch, "E124.17.2.0", {"start": v(301.52, -29.94) * mm, "end": v(299.02, -25.61) * mm});
            skLineSegment(sketch, "E124.2.3.0", {"start": v(309.2, -8) * mm, "end": v(309.2, -16) * mm});
            skLineSegment(sketch, "E124.5.3.0", {"start": v(314.2, -8) * mm, "end": v(309.2, -8) * mm});
            skLineSegment(sketch, "E124.8.3.0", {"start": v(309.2, -16) * mm, "end": v(311.66, -16) * mm});
            skLineSegment(sketch, "E124.11.3.0", {"start": v(309.2, 16) * mm, "end": v(311.66, 16) * mm});
            skLineSegment(sketch, "E124.14.3.0", {"start": v(309.2, 8) * mm, "end": v(309.2, 16) * mm});
            skLineSegment(sketch, "E124.17.3.0", {"start": v(314.2, 8) * mm, "end": v(309.2, 8) * mm});
            skLineSegment(sketch, "E125.2.4.0", {"start": v(299.02, 25.61) * mm, "end": v(305.95, 21.61) * mm});
            skLineSegment(sketch, "E125.5.4.0", {"start": v(301.52, 29.94) * mm, "end": v(299.02, 25.61) * mm});
            skLineSegment(sketch, "E125.8.4.0", {"start": v(305.95, 21.61) * mm, "end": v(307.19, 23.75) * mm});
            skLineSegment(sketch, "E125.11.4.0", {"start": v(278.24, 37.61) * mm, "end": v(279.47, 39.75) * mm});
            skLineSegment(sketch, "E125.14.4.0", {"start": v(285.17, 33.61) * mm, "end": v(278.24, 37.61) * mm});
            skLineSegment(sketch, "E125.17.4.0", {"start": v(287.67, 37.94) * mm, "end": v(285.17, 33.61) * mm});
            skLineSegment(sketch, "E126.2.5.0", {"start": v(264.83, 33.61) * mm, "end": v(271.76, 37.61) * mm});
            skLineSegment(sketch, "E126.5.5.0", {"start": v(262.33, 37.94) * mm, "end": v(264.83, 33.61) * mm});
            skLineSegment(sketch, "E126.8.5.0", {"start": v(271.76, 37.61) * mm, "end": v(270.53, 39.75) * mm});
            skLineSegment(sketch, "E126.11.5.0", {"start": v(244.05, 21.61) * mm, "end": v(242.81, 23.75) * mm});
            skLineSegment(sketch, "E126.14.5.0", {"start": v(250.98, 25.61) * mm, "end": v(244.05, 21.61) * mm});
            skLineSegment(sketch, "E126.17.5.0", {"start": v(248.48, 29.94) * mm, "end": v(250.98, 25.61) * mm});
            skArc(sketch, "E127.trimOffspring", {"start": v(279.47, 39.75) * mm, "mid": v(275, 40) * mm, "end": v(270.53, 39.75) * mm});
            skArc(sketch, "E128.trimOffspring", {"start": v(301.52, 29.94) * mm, "mid": v(295, 34.64) * mm, "end": v(287.67, 37.94) * mm});
            skArc(sketch, "E129.trimOffspring", {"start": v(311.66, 16) * mm, "mid": v(309.64, 20) * mm, "end": v(307.19, 23.75) * mm});
            skArc(sketch, "E130.trimOffspring", {"start": v(314.2, -8) * mm, "mid": v(315, 0) * mm, "end": v(314.2, 8) * mm});
            skArc(sketch, "E131.trimOffspring", {"start": v(307.19, -23.75) * mm, "mid": v(309.64, -20) * mm, "end": v(311.66, -16) * mm});
            skArc(sketch, "E132.trimOffspring", {"start": v(287.67, -37.94) * mm, "mid": v(295, -34.64) * mm, "end": v(301.52, -29.94) * mm});
            skArc(sketch, "E133.trimOffspring", {"start": v(270.53, -39.75) * mm, "mid": v(275, -40) * mm, "end": v(279.47, -39.75) * mm});
            skArc(sketch, "E134.trimOffspring", {"start": v(248.48, -29.94) * mm, "mid": v(255, -34.64) * mm, "end": v(262.33, -37.94) * mm});
            skSolve(sketch);
        }
        {
            var Q0;
            Q0=makeQuery(id+"F24.imprint","IMPRINT",FACE,{"disambiguationData":[TD([[makeQuery(id+"F24.imprint","IMPRINT",EDGE,{"derivedFrom":sQuery(id+"F24.wireOp",EDGE,"E109")}),1.0]])]});
            var Q1;
            Q1=sQuery(id+"F24.wireOp",EDGE,"E110");
            extrude(context, id + "F25", {"entities" : qUnion([Q0]), "surfaceEntities" : qUnion([Q1]), "depth" : 8 * mm, "offsetDistance" : 25 * mm});
        }
        {
            var Q0;
            Q0=qCreatedBy(makeId("Top.planeOp"),FACE);
            cPlane(context, id + "F26", {"entities" : qUnion([Q0]), "cplaneType" : CPlaneType.OFFSET, "offset" : 100 * mm, "oppositeDirection" : true, "width" : 150 * mm, "height" : 150 * mm});
        }
        {
            var Q0;
            Q0=makeQuery(id+"F25.opExtrude","SWEPT_BODY",BODY,{"disambiguationData":[OSD([sQuery(id+"F24.wireOp",EDGE,"E109"),sQuery(id+"F24.wireOp",EDGE,"E110"),sQuery(id+"F24.wireOp",EDGE,"E111"),sQuery(id+"F24.wireOp",EDGE,"E112.MirrorCS"),sQuery(id+"F24.wireOp",EDGE,"E113.MirrorCS"),sQuery(id+"F24.wireOp",EDGE,"E114.MirrorCS"),sQuery(id+"F24.wireOp",EDGE,"E115.1.1"),sQuery(id+"F24.wireOp",EDGE,"E115.1.2"),sQuery(id+"F24.wireOp",EDGE,"E115.1.3"),sQuery(id+"F24.wireOp",EDGE,"E115.1.4"),sQuery(id+"F24.wireOp",EDGE,"E115.1.5"),sQuery(id+"F24.wireOp",EDGE,"E115.1.6"),sQuery(id+"F24.wireOp",EDGE,"E115.2.0"),sQuery(id+"F24.wireOp",EDGE,"E115.2.1"),sQuery(id+"F24.wireOp",EDGE,"E115.2.2"),sQuery(id+"F24.wireOp",EDGE,"E115.2.3"),sQuery(id+"F24.wireOp",EDGE,"E115.2.4"),sQuery(id+"F24.wireOp",EDGE,"E115.2.5"),sQuery(id+"F24.wireOp",EDGE,"E115.2.6"),sQuery(id+"F24.wireOp",EDGE,"E116"),sQuery(id+"F24.wireOp",EDGE,"E117.trimOffspring"),sQuery(id+"F24.wireOp",EDGE,"E116"),sQuery(id+"F24.wireOp",EDGE,"E117.trimOffspring"),sQuery(id+"F24.wireOp",EDGE,"E118.trimOffspring"),sQuery(id+"F24.wireOp",EDGE,"E119.trimOffspring")])]});
            transform(context, id + "F27", {"entities" : qUnion([Q0]), "transformType" : TransformType.TRANSLATION_3D, "dx" : 2 * mm, "dy" : 0 * mm, "dz" : 0 * mm, "makeCopy" : false});
        }
        {
            var Q0;
            Q0=qCreatedBy(id+"F26.planeOp",FACE);
            var sketch = newSketch(context, id + "F28", { "sketchPlane" : qUnion([Q0])});
            skCircle(sketch, "E135", {"center": v(277, 0) * mm, "radius": 87.5 * mm});
            skArc(sketch, "E136", {"start": v(178.29, -16) * mm, "mid": v(190.4, -50) * mm, "end": v(213.79, -77.49) * mm});
            skLineSegment(sketch, "E137.0", {"start": v(177.32, -8) * mm, "end": v(182.32, -8) * mm});
            skLineSegment(sketch, "E138.0", {"start": v(182.32, -8) * mm, "end": v(182.32, -16) * mm});
            skLineSegment(sketch, "E139", {"start": v(182.32, -16) * mm, "end": v(178.29, -16) * mm});
            skLineSegment(sketch, "E140.MirrorCS", {"start": v(182.32, 8) * mm, "end": v(182.32, 16) * mm});
            skLineSegment(sketch, "E141.MirrorCS", {"start": v(182.32, 16) * mm, "end": v(178.29, 16) * mm});
            skLineSegment(sketch, "E142.MirrorCS", {"start": v(177.32, 8) * mm, "end": v(182.32, 8) * mm});
            skArc(sketch, "E143.trimOffspring", {"start": v(177.32, 8) * mm, "mid": v(177, 0) * mm, "end": v(177.32, -8) * mm});
            skLineSegment(sketch, "E144.1.0", {"start": v(222.73, -78) * mm, "end": v(215.8, -74) * mm});
            skLineSegment(sketch, "E144.1.1", {"start": v(215.8, -74) * mm, "end": v(213.79, -77.49) * mm});
            skLineSegment(sketch, "E144.1.2", {"start": v(220.23, -82.32) * mm, "end": v(222.73, -78) * mm});
            skLineSegment(sketch, "E144.1.3", {"start": v(234.09, -90.32) * mm, "end": v(236.59, -86) * mm});
            skLineSegment(sketch, "E144.1.4", {"start": v(236.59, -86) * mm, "end": v(243.52, -90) * mm});
            skLineSegment(sketch, "E144.1.5", {"start": v(243.52, -90) * mm, "end": v(241.5, -93.49) * mm});
            skLineSegment(sketch, "E144.2.0", {"start": v(317.41, -86) * mm, "end": v(310.48, -90) * mm});
            skLineSegment(sketch, "E144.2.1", {"start": v(310.48, -90) * mm, "end": v(312.5, -93.49) * mm});
            skLineSegment(sketch, "E144.2.2", {"start": v(319.91, -90.32) * mm, "end": v(317.41, -86) * mm});
            skLineSegment(sketch, "E144.2.3", {"start": v(333.77, -82.32) * mm, "end": v(331.27, -78) * mm});
            skLineSegment(sketch, "E144.2.4", {"start": v(331.27, -78) * mm, "end": v(338.2, -74) * mm});
            skLineSegment(sketch, "E144.2.5", {"start": v(338.2, -74) * mm, "end": v(340.21, -77.49) * mm});
            skArc(sketch, "E145.trimOffspring", {"start": v(213.79, 77.49) * mm, "mid": v(190.4, 50) * mm, "end": v(178.29, 16) * mm});
            skArc(sketch, "E146.trimOffspring", {"start": v(234.09, 90.32) * mm, "mid": v(227, 86.6) * mm, "end": v(220.23, 82.32) * mm});
            skArc(sketch, "E147.trimOffspring", {"start": v(241.5, -93.49) * mm, "mid": v(277, -100) * mm, "end": v(312.5, -93.49) * mm});
            skArc(sketch, "E148.trimOffspring", {"start": v(220.23, -82.32) * mm, "mid": v(227, -86.6) * mm, "end": v(234.09, -90.32) * mm});
            skCircle(sketch, "E149.0", {"center": v(277, 0) * mm, "radius": 22 * mm, "construction": true});
            skLineSegment(sketch, "E150.3.3.0", {"start": v(371.68, -16) * mm, "end": v(375.71, -16) * mm});
            skLineSegment(sketch, "E150.6.3.0", {"start": v(376.68, -8) * mm, "end": v(371.68, -8) * mm});
            skLineSegment(sketch, "E150.9.3.0", {"start": v(376.68, 8) * mm, "end": v(371.68, 8) * mm});
            skLineSegment(sketch, "E150.12.3.0", {"start": v(371.68, 8) * mm, "end": v(371.68, 16) * mm});
            skLineSegment(sketch, "E150.15.3.0", {"start": v(371.68, 16) * mm, "end": v(375.71, 16) * mm});
            skLineSegment(sketch, "E150.17.3.0", {"start": v(371.68, -8) * mm, "end": v(371.68, -16) * mm});
            skLineSegment(sketch, "E151", {"start": v(277, -123.32) * mm, "end": v(277, 151.48) * mm, "construction": true});
            skLineSegment(sketch, "E152.3.4.0", {"start": v(338.2, 74) * mm, "end": v(340.21, 77.49) * mm});
            skLineSegment(sketch, "E152.6.4.0", {"start": v(333.77, 82.32) * mm, "end": v(331.27, 78) * mm});
            skLineSegment(sketch, "E152.9.4.0", {"start": v(319.91, 90.32) * mm, "end": v(317.41, 86) * mm});
            skLineSegment(sketch, "E152.12.4.0", {"start": v(317.41, 86) * mm, "end": v(310.48, 90) * mm});
            skLineSegment(sketch, "E152.15.4.0", {"start": v(310.48, 90) * mm, "end": v(312.5, 93.49) * mm});
            skLineSegment(sketch, "E152.17.4.0", {"start": v(331.27, 78) * mm, "end": v(338.2, 74) * mm});
            skLineSegment(sketch, "E153.3.5.0", {"start": v(243.52, 90) * mm, "end": v(241.5, 93.49) * mm});
            skLineSegment(sketch, "E153.6.5.0", {"start": v(234.09, 90.32) * mm, "end": v(236.59, 86) * mm});
            skLineSegment(sketch, "E153.9.5.0", {"start": v(220.23, 82.32) * mm, "end": v(222.73, 78) * mm});
            skLineSegment(sketch, "E153.12.5.0", {"start": v(222.73, 78) * mm, "end": v(215.8, 74) * mm});
            skLineSegment(sketch, "E153.15.5.0", {"start": v(215.8, 74) * mm, "end": v(213.79, 77.49) * mm});
            skLineSegment(sketch, "E153.17.5.0", {"start": v(236.59, 86) * mm, "end": v(243.52, 90) * mm});
            skArc(sketch, "E154.trimOffspring", {"start": v(312.5, 93.49) * mm, "mid": v(277, 100) * mm, "end": v(241.5, 93.49) * mm});
            skArc(sketch, "E155.trimOffspring", {"start": v(333.77, 82.32) * mm, "mid": v(327, 86.6) * mm, "end": v(319.91, 90.32) * mm});
            skArc(sketch, "E156.trimOffspring", {"start": v(375.71, 16) * mm, "mid": v(363.6, 50) * mm, "end": v(340.21, 77.49) * mm});
            skArc(sketch, "E157.trimOffspring", {"start": v(376.68, -8) * mm, "mid": v(377, 0) * mm, "end": v(376.68, 8) * mm});
            skArc(sketch, "E158.trimOffspring", {"start": v(340.21, -77.49) * mm, "mid": v(363.6, -50) * mm, "end": v(375.71, -16) * mm});
            skArc(sketch, "E159.trimOffspring", {"start": v(319.91, -90.32) * mm, "mid": v(327, -86.6) * mm, "end": v(333.77, -82.32) * mm});
            skSolve(sketch);
        }
        {
            var Q0;
            Q0=qSketchRegion(id+"F28",true);
            extrude(context, id + "F29", {"entities" : qUnion([Q0]), "oppositeDirection" : true, "depth" : 8 * mm, "offsetDistance" : 25 * mm});
        }
        {
            var Q0;
            Q0=makeQuery(id+"F20.opExtrude","CAP_FACE",FACE,{"disambiguationData":[OSD([sQuery(id+"F19.wireOp",EDGE,"E86.top"),sQuery(id+"F19.wireOp",EDGE,"E86.left"),sQuery(id+"F19.wireOp",EDGE,"E86.right"),sQuery(id+"F19.wireOp",EDGE,"E89.MirrorC"),sQuery(id+"F19.wireOp",EDGE,"E90.filletArc"),sQuery(id+"F19.wireOp",EDGE,"E91.filletArc"),sQuery(id+"F19.wireOp",EDGE,"E92.bottom"),sQuery(id+"F19.wireOp",EDGE,"E93"),sQuery(id+"F19.wireOp",EDGE,"E94.filletArc"),sQuery(id+"F19.wireOp",EDGE,"E95.filletArc")])],"isStart":false});
            var sketch = newSketch(context, id + "F30", { "sketchPlane" : qUnion([Q0])});
            skLineSegment(sketch, "E160.top", {"start": v(170, -5) * mm, "end": v(170, 5) * mm});
            skLineSegment(sketch, "E160.left", {"start": v(191.07, -10) * mm, "end": v(175, -10) * mm});
            skLineSegment(sketch, "E160.right", {"start": v(203.17, 10) * mm, "end": v(175, 10) * mm});
            skCircle(sketch, "E161.MirrorC", {"center": v(180, 0) * mm, "radius": 5 * mm});
            skPoint(sketch, "E162.visualSharp", {"position": v(170, -10) * mm});
            skArc(sketch, "E162.filletArc", {"start": v(170, -5) * mm, "mid": v(171.46, -8.54) * mm, "end": v(175, -10) * mm});
            skPoint(sketch, "E163.visualSharp", {"position": v(170, 10) * mm});
            skArc(sketch, "E163.filletArc", {"start": v(175, 10) * mm, "mid": v(171.46, 8.54) * mm, "end": v(170, 5) * mm});
            skLineSegment(sketch, "E164", {"start": v(237.8, 100) * mm, "end": v(212.74, 17.1) * mm});
            skLineSegment(sketch, "E165.trimOffspring", {"start": v(200.64, -22.9) * mm, "end": v(177.32, -100) * mm});
            skLineSegment(sketch, "E166", {"start": v(237.8, 100) * mm, "end": v(237.8, 115) * mm});
            skLineSegment(sketch, "E167", {"start": v(242.8, 120) * mm, "end": v(242.8, 120) * mm});
            skLineSegment(sketch, "E168", {"start": v(247.8, 115) * mm, "end": v(247.8, 108) * mm});
            skLineSegment(sketch, "E169", {"start": v(182.32, -120) * mm, "end": v(182.32, -120) * mm});
            skLineSegment(sketch, "E170.0.2", {"start": v(242.8, 108) * mm, "end": v(237.8, 108) * mm, "construction": true});
            skLineSegment(sketch, "E170.0.3", {"start": v(237.8, 108) * mm, "end": v(237.8, 100) * mm, "construction": true});
            skPoint(sketch, "E171.visualSharp", {"position": v(210.59, 10) * mm});
            skArc(sketch, "E171.filletArc", {"start": v(203.17, 10) * mm, "mid": v(209.13, 11.97) * mm, "end": v(212.74, 17.1) * mm});
            skPoint(sketch, "E172.visualSharp", {"position": v(204.54, -10) * mm});
            skArc(sketch, "E172.filletArc", {"start": v(200.64, -22.9) * mm, "mid": v(199.1, -14.04) * mm, "end": v(191.07, -10) * mm});
            skPoint(sketch, "E173.visualSharp", {"position": v(177.32, -120) * mm});
            skArc(sketch, "E173.filletArc", {"start": v(177.32, -115) * mm, "mid": v(178.78, -118.54) * mm, "end": v(182.32, -120) * mm});
            skPoint(sketch, "E174.visualSharp", {"position": v(187.32, -120) * mm});
            skArc(sketch, "E174.filletArc", {"start": v(182.32, -120) * mm, "mid": v(185.86, -118.54) * mm, "end": v(187.32, -115) * mm});
            skPoint(sketch, "E175.visualSharp", {"position": v(237.8, 120) * mm});
            skArc(sketch, "E175.filletArc", {"start": v(242.8, 120) * mm, "mid": v(239.27, 118.54) * mm, "end": v(237.8, 115) * mm});
            skPoint(sketch, "E176.visualSharp", {"position": v(247.8, 120) * mm});
            skArc(sketch, "E176.filletArc", {"start": v(247.8, 115) * mm, "mid": v(246.34, 118.54) * mm, "end": v(242.8, 120) * mm});
            skLineSegment(sketch, "E177", {"start": v(247.8, 108) * mm, "end": v(242.8, 108) * mm});
            skLineSegment(sketch, "E178", {"start": v(242.8, 108) * mm, "end": v(242.8, 100) * mm});
            skLineSegment(sketch, "E179", {"start": v(242.8, 100) * mm, "end": v(247.8, 100) * mm});
            skLineSegment(sketch, "E180", {"start": v(187.32, -100) * mm, "end": v(182.32, -100) * mm});
            skLineSegment(sketch, "E181", {"start": v(182.32, -100) * mm, "end": v(182.32, -108) * mm});
            skLineSegment(sketch, "E182", {"start": v(182.32, -108) * mm, "end": v(187.32, -108) * mm});
            skLineSegment(sketch, "E183.0.0", {"start": v(182.32, -100) * mm, "end": v(177.32, -100) * mm, "construction": true});
            skLineSegment(sketch, "E183.0.1", {"start": v(177.32, -100) * mm, "end": v(177.32, -108) * mm, "construction": true});
            skLineSegment(sketch, "E183.0.2", {"start": v(177.32, -108) * mm, "end": v(182.32, -108) * mm, "construction": true});
            skLineSegment(sketch, "E183.0.3", {"start": v(182.32, -108) * mm, "end": v(182.32, -100) * mm, "construction": true});
            skLineSegment(sketch, "E184", {"start": v(177.32, -100) * mm, "end": v(177.32, -115) * mm});
            skLineSegment(sketch, "E185", {"start": v(187.32, -108) * mm, "end": v(187.32, -115) * mm});
            skLineSegment(sketch, "E186", {"start": v(247.8, 100) * mm, "end": v(233.9, 54) * mm});
            skLineSegment(sketch, "E187", {"start": v(183.65, 50) * mm, "end": v(298.64, 50) * mm, "construction": true});
            skLineSegment(sketch, "E188", {"start": v(172.05, 0) * mm, "end": v(324.48, 0) * mm, "construction": true});
            skLineSegment(sketch, "E189", {"start": v(155.59, -50) * mm, "end": v(297.84, -50) * mm, "construction": true});
            skLineSegment(sketch, "E190", {"start": v(233.9, 54) * mm, "end": v(228.9, 54) * mm});
            skLineSegment(sketch, "E191", {"start": v(228.9, 54) * mm, "end": v(228.9, 46) * mm});
            skLineSegment(sketch, "E192", {"start": v(228.9, 46) * mm, "end": v(231.49, 46) * mm});
            skLineSegment(sketch, "E193", {"start": v(218.8, 4) * mm, "end": v(213.8, 4) * mm});
            skLineSegment(sketch, "E194", {"start": v(213.8, 4) * mm, "end": v(213.8, -4) * mm});
            skLineSegment(sketch, "E195", {"start": v(213.8, -4) * mm, "end": v(216.35, -4) * mm});
            skLineSegment(sketch, "E196", {"start": v(203.65, -46) * mm, "end": v(198.65, -46) * mm});
            skLineSegment(sketch, "E197", {"start": v(198.65, -46) * mm, "end": v(198.65, -54) * mm});
            skLineSegment(sketch, "E198", {"start": v(198.65, -54) * mm, "end": v(201.23, -54) * mm});
            skLineSegment(sketch, "E199.trimOffspring", {"start": v(201.23, -54) * mm, "end": v(187.32, -100) * mm});
            skLineSegment(sketch, "E200.trimOffspring", {"start": v(216.35, -4) * mm, "end": v(203.65, -46) * mm});
            skLineSegment(sketch, "E201.trimOffspring", {"start": v(231.48, 46) * mm, "end": v(218.77, 4) * mm});
            skSolve(sketch);
        }
        {
            var Q0;
            Q0=qSketchRegion(id+"F30",true);
            extrude(context, id + "F31", {"entities" : qUnion([Q0]), "depth" : 8 * mm, "offsetDistance" : 25 * mm});
        }
        {
            var Q0;
            Q0=makeQuery(id+"F31.opExtrude","SWEPT_BODY",BODY,{"disambiguationData":[OSD([sQuery(id+"F30.wireOp",EDGE,"E160.top"),sQuery(id+"F30.wireOp",EDGE,"E160.left"),sQuery(id+"F30.wireOp",EDGE,"E160.right"),sQuery(id+"F30.wireOp",EDGE,"E161.MirrorC"),sQuery(id+"F30.wireOp",EDGE,"E162.filletArc"),sQuery(id+"F30.wireOp",EDGE,"E163.filletArc"),sQuery(id+"F30.wireOp",EDGE,"E164"),sQuery(id+"F30.wireOp",EDGE,"E165.trimOffspring"),sQuery(id+"F30.wireOp",EDGE,"E166"),sQuery(id+"F30.wireOp",EDGE,"E168"),sQuery(id+"F30.wireOp",EDGE,"xNdozj4u-sUJ1-z0ST-gP8R-Wofgr4fJZpDs"),sQuery(id+"F30.wireOp",EDGE,"vQYsRbkT-yidu-s9Dx-8HfP-1cVZBKzJqOnp"),sQuery(id+"F30.wireOp",EDGE,"Z77I2Dmk-SxWq-cxIy-LfgW-7D05WhU1y4ug"),sQuery(id+"F30.wireOp",EDGE,"6ed29332-a8b3-43e6-a333-3f3c8759dfa2"),sQuery(id+"F30.wireOp",EDGE,"E171.filletArc"),sQuery(id+"F30.wireOp",EDGE,"E172.filletArc"),sQuery(id+"F30.wireOp",EDGE,"E173.filletArc"),sQuery(id+"F30.wireOp",EDGE,"E174.filletArc"),sQuery(id+"F30.wireOp",EDGE,"E175.filletArc"),sQuery(id+"F30.wireOp",EDGE,"E176.filletArc"),sQuery(id+"F30.wireOp",EDGE,"E177"),sQuery(id+"F30.wireOp",EDGE,"E178"),sQuery(id+"F30.wireOp",EDGE,"E179"),sQuery(id+"F30.wireOp",EDGE,"E180"),sQuery(id+"F30.wireOp",EDGE,"E181"),sQuery(id+"F30.wireOp",EDGE,"E182")])]});
            var Q1;
            Q1=qCreatedBy(makeId("Front.planeOp"),FACE);
            mirror(context, id + "F32", {"entities" : qUnion([Q0]), "mirrorPlane" : qUnion([Q1])});
        }
        {
            var Q0;
            Q0=makeQuery(id+"F25.opExtrude","SWEPT_FACE",FACE,{"disambiguationData":[OSD([sQuery(id+"F24.wireOp",EDGE,"E115.1.6")])]});
            var sketch = newSketch(context, id + "F33", { "sketchPlane" : qUnion([Q0])});
            skLineSegment(sketch, "E202", {"start": v(99.3, 100) * mm, "end": v(99.3, 115) * mm});
            skLineSegment(sketch, "E203", {"start": v(109.3, 115) * mm, "end": v(109.3, 108) * mm});
            skLineSegment(sketch, "E204", {"start": v(109.3, 100) * mm, "end": v(95.4, 54) * mm});
            skLineSegment(sketch, "E205.0.3", {"start": v(99.3, 108) * mm, "end": v(99.3, 100) * mm, "construction": true});
            skArc(sketch, "E206.filletArc", {"start": v(38.82, -115) * mm, "mid": v(40.28, -118.54) * mm, "end": v(43.82, -120) * mm});
            skArc(sketch, "E207.filletArc", {"start": v(43.82, -120) * mm, "mid": v(47.36, -118.54) * mm, "end": v(48.82, -115) * mm});
            skPoint(sketch, "E208.visualSharp", {"position": v(99.3, 120) * mm});
            skArc(sketch, "E208.filletArc", {"start": v(104.3, 120) * mm, "mid": v(100.77, 118.54) * mm, "end": v(99.3, 115) * mm});
            skPoint(sketch, "E209.visualSharp", {"position": v(109.3, 120) * mm});
            skArc(sketch, "E209.filletArc", {"start": v(109.3, 115) * mm, "mid": v(107.84, 118.54) * mm, "end": v(104.3, 120) * mm});
            skLineSegment(sketch, "E210", {"start": v(109.3, 108) * mm, "end": v(104.3, 108) * mm});
            skLineSegment(sketch, "E211", {"start": v(104.3, 108) * mm, "end": v(104.3, 100) * mm});
            skLineSegment(sketch, "E212", {"start": v(104.3, 100) * mm, "end": v(109.3, 100) * mm});
            skLineSegment(sketch, "E213", {"start": v(48.82, -100) * mm, "end": v(43.82, -100) * mm});
            skLineSegment(sketch, "E214", {"start": v(43.82, -100) * mm, "end": v(43.82, -108) * mm});
            skLineSegment(sketch, "E215", {"start": v(43.82, -108) * mm, "end": v(48.82, -108) * mm});
            skLineSegment(sketch, "E216.0.0", {"start": v(43.82, -100) * mm, "end": v(38.82, -100) * mm, "construction": true});
            skLineSegment(sketch, "E216.0.1", {"start": v(38.82, -100) * mm, "end": v(38.82, -108) * mm});
            skLineSegment(sketch, "E216.0.2", {"start": v(38.82, -108) * mm, "end": v(43.82, -108) * mm, "construction": true});
            skLineSegment(sketch, "E216.0.3", {"start": v(43.82, -108) * mm, "end": v(43.82, -100) * mm, "construction": true});
            skLineSegment(sketch, "E217", {"start": v(48.82, -108) * mm, "end": v(48.82, -115) * mm});
            skLineSegment(sketch, "E218", {"start": v(99.3, 100) * mm, "end": v(38.82, -100) * mm});
            skPoint(sketch, "E219.0", {"position": v(104.3, 108) * mm});
            skLineSegment(sketch, "E220", {"start": v(38.82, -108) * mm, "end": v(38.82, -115) * mm});
            skLineSegment(sketch, "E221", {"start": v(45.15, 50) * mm, "end": v(160.14, 50) * mm, "construction": true});
            skLineSegment(sketch, "E222", {"start": v(33.55, 0) * mm, "end": v(185.98, 0) * mm, "construction": true});
            skLineSegment(sketch, "E223", {"start": v(17.09, -50) * mm, "end": v(159.34, -50) * mm, "construction": true});
            skLineSegment(sketch, "E224", {"start": v(95.4, 54) * mm, "end": v(90.4, 54) * mm});
            skLineSegment(sketch, "E225", {"start": v(90.4, 54) * mm, "end": v(90.4, 46) * mm});
            skLineSegment(sketch, "E226", {"start": v(90.4, 46) * mm, "end": v(92.99, 46) * mm});
            skLineSegment(sketch, "E227", {"start": v(80.3, 4) * mm, "end": v(75.3, 4) * mm});
            skLineSegment(sketch, "E228", {"start": v(75.3, 4) * mm, "end": v(75.3, -4) * mm});
            skLineSegment(sketch, "E229", {"start": v(75.3, -4) * mm, "end": v(77.85, -4) * mm});
            skLineSegment(sketch, "E230", {"start": v(65.15, -46) * mm, "end": v(60.15, -46) * mm});
            skLineSegment(sketch, "E231", {"start": v(60.15, -46) * mm, "end": v(60.15, -54) * mm});
            skLineSegment(sketch, "E232", {"start": v(60.15, -54) * mm, "end": v(62.73, -54) * mm});
            skLineSegment(sketch, "E233.trimOffspring", {"start": v(62.73, -54) * mm, "end": v(48.82, -100) * mm});
            skLineSegment(sketch, "E234.trimOffspring", {"start": v(77.85, -4) * mm, "end": v(65.15, -46) * mm});
            skLineSegment(sketch, "E235.trimOffspring", {"start": v(92.98, 46) * mm, "end": v(80.27, 4) * mm});
            skSolve(sketch);
        }
        {
            var Q0;
            Q0=qSketchRegion(id+"F33",true);
            extrude(context, id + "F34", {"entities" : qUnion([Q0]), "depth" : 8 * mm, "offsetDistance" : 25 * mm});
        }
        {
            var Q0;
            Q0=makeQuery(id+"F34.opExtrude","CAP_FACE",FACE,{"disambiguationData":[OSD([sQuery(id+"F33.wireOp",EDGE,"E202"),sQuery(id+"F33.wireOp",EDGE,"E203"),sQuery(id+"F33.wireOp",EDGE,"E204"),sQuery(id+"F33.wireOp",EDGE,"E206.filletArc"),sQuery(id+"F33.wireOp",EDGE,"E207.filletArc"),sQuery(id+"F33.wireOp",EDGE,"E208.filletArc"),sQuery(id+"F33.wireOp",EDGE,"E209.filletArc"),sQuery(id+"F33.wireOp",EDGE,"E210"),sQuery(id+"F33.wireOp",EDGE,"E211"),sQuery(id+"F33.wireOp",EDGE,"E212"),sQuery(id+"F33.wireOp",EDGE,"E213"),sQuery(id+"F33.wireOp",EDGE,"E214"),sQuery(id+"F33.wireOp",EDGE,"E216.0.1"),sQuery(id+"F33.wireOp",EDGE,"E215"),sQuery(id+"F33.wireOp",EDGE,"E217"),sQuery(id+"F33.wireOp",EDGE,"E218"),sQuery(id+"F33.wireOp",EDGE,"E220")])],"isStart":true});
            cPlane(context, id + "F35", {"entities" : qUnion([Q0]), "cplaneType" : CPlaneType.OFFSET, "offset" : 8 * mm, "width" : 150 * mm, "height" : 150 * mm});
        }
        {
            var Q0;
            Q0=makeQuery(id+"F34.opExtrude","SWEPT_BODY",BODY,{"disambiguationData":[OSD([sQuery(id+"F33.wireOp",EDGE,"E202"),sQuery(id+"F33.wireOp",EDGE,"E203"),sQuery(id+"F33.wireOp",EDGE,"E204"),sQuery(id+"F33.wireOp",EDGE,"E206.filletArc"),sQuery(id+"F33.wireOp",EDGE,"E207.filletArc"),sQuery(id+"F33.wireOp",EDGE,"E208.filletArc"),sQuery(id+"F33.wireOp",EDGE,"E209.filletArc"),sQuery(id+"F33.wireOp",EDGE,"E210"),sQuery(id+"F33.wireOp",EDGE,"E211"),sQuery(id+"F33.wireOp",EDGE,"E212"),sQuery(id+"F33.wireOp",EDGE,"E213"),sQuery(id+"F33.wireOp",EDGE,"E214"),sQuery(id+"F33.wireOp",EDGE,"E216.0.1"),sQuery(id+"F33.wireOp",EDGE,"E215"),sQuery(id+"F33.wireOp",EDGE,"E217"),sQuery(id+"F33.wireOp",EDGE,"E218"),sQuery(id+"F33.wireOp",EDGE,"E220")])]});
            var Q1;
            Q1=qCreatedBy(id+"F35.planeOp",FACE);
            mirror(context, id + "F36", {"entities" : qUnion([Q0]), "mirrorPlane" : qUnion([Q1])});
        }
        {
            var Q0;
            Q0=makeQuery(id+"F34.opExtrude","SWEPT_BODY",BODY,{"disambiguationData":[OSD([sQuery(id+"F33.wireOp",EDGE,"E202"),sQuery(id+"F33.wireOp",EDGE,"E203"),sQuery(id+"F33.wireOp",EDGE,"E204"),sQuery(id+"F33.wireOp",EDGE,"E206.filletArc"),sQuery(id+"F33.wireOp",EDGE,"E207.filletArc"),sQuery(id+"F33.wireOp",EDGE,"E208.filletArc"),sQuery(id+"F33.wireOp",EDGE,"E209.filletArc"),sQuery(id+"F33.wireOp",EDGE,"E210"),sQuery(id+"F33.wireOp",EDGE,"E211"),sQuery(id+"F33.wireOp",EDGE,"E212"),sQuery(id+"F33.wireOp",EDGE,"E213"),sQuery(id+"F33.wireOp",EDGE,"E214"),sQuery(id+"F33.wireOp",EDGE,"E216.0.1"),sQuery(id+"F33.wireOp",EDGE,"E215"),sQuery(id+"F33.wireOp",EDGE,"E217"),sQuery(id+"F33.wireOp",EDGE,"E218"),sQuery(id+"F33.wireOp",EDGE,"E220")])]});
            var Q1;
            Q1=makeQuery(id+"F36.opPattern","COPY",BODY,{"derivedFrom":makeQuery(id+"F34.opExtrude","SWEPT_BODY",BODY,{"disambiguationData":[OSD([sQuery(id+"F33.wireOp",EDGE,"E202"),sQuery(id+"F33.wireOp",EDGE,"E203"),sQuery(id+"F33.wireOp",EDGE,"E204"),sQuery(id+"F33.wireOp",EDGE,"E206.filletArc"),sQuery(id+"F33.wireOp",EDGE,"E207.filletArc"),sQuery(id+"F33.wireOp",EDGE,"E208.filletArc"),sQuery(id+"F33.wireOp",EDGE,"E209.filletArc"),sQuery(id+"F33.wireOp",EDGE,"E210"),sQuery(id+"F33.wireOp",EDGE,"E211"),sQuery(id+"F33.wireOp",EDGE,"E212"),sQuery(id+"F33.wireOp",EDGE,"E213"),sQuery(id+"F33.wireOp",EDGE,"E214"),sQuery(id+"F33.wireOp",EDGE,"E216.0.1"),sQuery(id+"F33.wireOp",EDGE,"E215"),sQuery(id+"F33.wireOp",EDGE,"E217"),sQuery(id+"F33.wireOp",EDGE,"E218"),sQuery(id+"F33.wireOp",EDGE,"E220")])]}),"instanceName":"1"});
            var Q2;
            Q2=makeQuery(id+"F25.opExtrude","CAP_EDGE",EDGE,{"disambiguationData":[OSD([sQuery(id+"F24.wireOp",EDGE,"E107")])],"isStart":false});
            circularPattern(context, id + "F37", {"entities" : qUnion([Q0, Q1]), "axis" : qUnion([Q2]), "angle" : 360 * degree, "instanceCount" : 6, "equalSpace" : true});
        }
        {
            var Q0;
            Q0=makeQuery(id+"F37.opPattern","COPY",BODY,{"derivedFrom":makeQuery(id+"F34.opExtrude","SWEPT_BODY",BODY,{"disambiguationData":[OSD([sQuery(id+"F33.wireOp",EDGE,"E202"),sQuery(id+"F33.wireOp",EDGE,"E203"),sQuery(id+"F33.wireOp",EDGE,"E204"),sQuery(id+"F33.wireOp",EDGE,"E206.filletArc"),sQuery(id+"F33.wireOp",EDGE,"E207.filletArc"),sQuery(id+"F33.wireOp",EDGE,"E208.filletArc"),sQuery(id+"F33.wireOp",EDGE,"E209.filletArc"),sQuery(id+"F33.wireOp",EDGE,"E210"),sQuery(id+"F33.wireOp",EDGE,"E211"),sQuery(id+"F33.wireOp",EDGE,"E212"),sQuery(id+"F33.wireOp",EDGE,"E213"),sQuery(id+"F33.wireOp",EDGE,"E214"),sQuery(id+"F33.wireOp",EDGE,"E216.0.1"),sQuery(id+"F33.wireOp",EDGE,"E215"),sQuery(id+"F33.wireOp",EDGE,"E217"),sQuery(id+"F33.wireOp",EDGE,"E218"),sQuery(id+"F33.wireOp",EDGE,"E220")])]}),"instanceName":"5"});
            var Q1;
            Q1=makeQuery(id+"F37.opPattern","COPY",BODY,{"derivedFrom":makeQuery(id+"F36.opPattern","COPY",BODY,{"derivedFrom":makeQuery(id+"F34.opExtrude","SWEPT_BODY",BODY,{"disambiguationData":[OSD([sQuery(id+"F33.wireOp",EDGE,"E202"),sQuery(id+"F33.wireOp",EDGE,"E203"),sQuery(id+"F33.wireOp",EDGE,"E204"),sQuery(id+"F33.wireOp",EDGE,"E206.filletArc"),sQuery(id+"F33.wireOp",EDGE,"E207.filletArc"),sQuery(id+"F33.wireOp",EDGE,"E208.filletArc"),sQuery(id+"F33.wireOp",EDGE,"E209.filletArc"),sQuery(id+"F33.wireOp",EDGE,"E210"),sQuery(id+"F33.wireOp",EDGE,"E211"),sQuery(id+"F33.wireOp",EDGE,"E212"),sQuery(id+"F33.wireOp",EDGE,"E213"),sQuery(id+"F33.wireOp",EDGE,"E214"),sQuery(id+"F33.wireOp",EDGE,"E216.0.1"),sQuery(id+"F33.wireOp",EDGE,"E215"),sQuery(id+"F33.wireOp",EDGE,"E217"),sQuery(id+"F33.wireOp",EDGE,"E218"),sQuery(id+"F33.wireOp",EDGE,"E220")])]}),"instanceName":"1"}),"instanceName":"5"});
            deleteBodies(context, id + "F38", {"entities" : qUnion([Q0, Q1])});
        }
        {
            var Q0;
            Q0=makeQuery(id+"F31.opExtrude","SWEPT_FACE",FACE,{"disambiguationData":[OSD([sQuery(id+"F30.wireOp",EDGE,"E192")])]});
            cPlane(context, id + "F39", {"entities" : qUnion([Q0]), "cplaneType" : CPlaneType.OFFSET, "offset" : 0 * mm, "width" : 150 * mm, "height" : 150 * mm});
        }
        {
            var Q0;
            Q0=qCreatedBy(id+"F39.planeOp",FACE);
            var sketch = newSketch(context, id + "F40", { "sketchPlane" : qUnion([Q0])});
            skCircle(sketch, "E236.0", {"center": v(277, 0) * mm, "radius": 22 * mm, "construction": true});
            skArc(sketch, "E237", {"start": v(223.33, 8) * mm, "mid": v(222.74, 0) * mm, "end": v(223.33, -8) * mm});
            skCircle(sketch, "E238", {"center": v(277, 0) * mm, "radius": 41.76 * mm});
            skLineSegment(sketch, "E239", {"start": v(264.62, 0) * mm, "end": v(206.1, 0) * mm, "construction": true});
            skLineSegment(sketch, "E240", {"start": v(223.33, -8) * mm, "end": v(229.33, -8) * mm});
            skLineSegment(sketch, "E241", {"start": v(229.33, -8) * mm, "end": v(229.33, -16) * mm});
            skLineSegment(sketch, "E242", {"start": v(229.33, -16) * mm, "end": v(225.15, -16) * mm});
            skLineSegment(sketch, "E243.MirrorCS", {"start": v(229.33, 16) * mm, "end": v(225.15, 16) * mm});
            skLineSegment(sketch, "E244.MirrorCS", {"start": v(223.33, 8) * mm, "end": v(229.33, 8) * mm});
            skLineSegment(sketch, "E245.MirrorCS", {"start": v(229.33, 8) * mm, "end": v(229.33, 16) * mm});
            skArc(sketch, "E246.trimOffspring", {"start": v(225.15, -16) * mm, "mid": v(230, -27.13) * mm, "end": v(237.22, -36.9) * mm});
            skLineSegment(sketch, "E247.1.0", {"start": v(239.3, -33.28) * mm, "end": v(237.22, -36.9) * mm});
            skLineSegment(sketch, "E247.1.1", {"start": v(246.24, -37.28) * mm, "end": v(239.3, -33.28) * mm});
            skLineSegment(sketch, "E247.1.2", {"start": v(243.24, -42.48) * mm, "end": v(246.24, -37.28) * mm});
            skLineSegment(sketch, "E247.1.3", {"start": v(257.1, -50.48) * mm, "end": v(260.1, -45.28) * mm});
            skLineSegment(sketch, "E247.1.4", {"start": v(260.1, -45.28) * mm, "end": v(267.02, -49.28) * mm});
            skLineSegment(sketch, "E247.1.5", {"start": v(267.02, -49.28) * mm, "end": v(264.93, -52.9) * mm});
            skLineSegment(sketch, "E247.2.0", {"start": v(286.98, -49.28) * mm, "end": v(289.07, -52.9) * mm});
            skLineSegment(sketch, "E247.2.1", {"start": v(293.9, -45.28) * mm, "end": v(286.98, -49.28) * mm});
            skLineSegment(sketch, "E247.2.2", {"start": v(296.9, -50.48) * mm, "end": v(293.9, -45.28) * mm});
            skLineSegment(sketch, "E247.2.3", {"start": v(310.76, -42.48) * mm, "end": v(307.76, -37.28) * mm});
            skLineSegment(sketch, "E247.2.4", {"start": v(307.76, -37.28) * mm, "end": v(314.7, -33.28) * mm});
            skLineSegment(sketch, "E247.2.5", {"start": v(314.7, -33.28) * mm, "end": v(316.78, -36.9) * mm});
            skLineSegment(sketch, "E247.3.0", {"start": v(324.67, -16) * mm, "end": v(328.85, -16) * mm});
            skLineSegment(sketch, "E247.3.1", {"start": v(324.67, -8) * mm, "end": v(324.67, -16) * mm});
            skLineSegment(sketch, "E247.3.2", {"start": v(330.67, -8) * mm, "end": v(324.67, -8) * mm});
            skLineSegment(sketch, "E247.3.3", {"start": v(330.67, 8) * mm, "end": v(324.67, 8) * mm});
            skLineSegment(sketch, "E247.3.4", {"start": v(324.67, 8) * mm, "end": v(324.67, 16) * mm});
            skLineSegment(sketch, "E247.3.5", {"start": v(324.67, 16) * mm, "end": v(328.85, 16) * mm});
            skLineSegment(sketch, "E247.4.0", {"start": v(314.7, 33.28) * mm, "end": v(316.78, 36.9) * mm});
            skLineSegment(sketch, "E247.4.1", {"start": v(307.76, 37.28) * mm, "end": v(314.7, 33.28) * mm});
            skLineSegment(sketch, "E247.4.2", {"start": v(310.76, 42.48) * mm, "end": v(307.76, 37.28) * mm});
            skLineSegment(sketch, "E247.4.3", {"start": v(296.9, 50.48) * mm, "end": v(293.9, 45.28) * mm});
            skLineSegment(sketch, "E247.4.4", {"start": v(293.9, 45.28) * mm, "end": v(286.98, 49.28) * mm});
            skLineSegment(sketch, "E247.4.5", {"start": v(286.98, 49.28) * mm, "end": v(289.07, 52.9) * mm});
            skLineSegment(sketch, "E247.5.0", {"start": v(267.02, 49.28) * mm, "end": v(264.93, 52.9) * mm});
            skLineSegment(sketch, "E247.5.1", {"start": v(260.1, 45.28) * mm, "end": v(267.02, 49.28) * mm});
            skLineSegment(sketch, "E247.5.2", {"start": v(257.1, 50.48) * mm, "end": v(260.1, 45.28) * mm});
            skLineSegment(sketch, "E247.5.3", {"start": v(243.24, 42.48) * mm, "end": v(246.24, 37.28) * mm});
            skLineSegment(sketch, "E247.5.4", {"start": v(246.24, 37.28) * mm, "end": v(239.3, 33.28) * mm});
            skLineSegment(sketch, "E247.5.5", {"start": v(239.3, 33.28) * mm, "end": v(237.22, 36.9) * mm});
            skArc(sketch, "E248.trimOffspring", {"start": v(237.22, 36.9) * mm, "mid": v(230, 27.13) * mm, "end": v(225.15, 16) * mm});
            skArc(sketch, "E249.trimOffspring", {"start": v(257.1, 50.48) * mm, "mid": v(249.87, 47) * mm, "end": v(243.24, 42.48) * mm});
            skArc(sketch, "E250.trimOffspring", {"start": v(289.07, 52.9) * mm, "mid": v(277, 54.26) * mm, "end": v(264.93, 52.9) * mm});
            skArc(sketch, "E251.trimOffspring", {"start": v(310.76, 42.48) * mm, "mid": v(304.13, 47) * mm, "end": v(296.9, 50.48) * mm});
            skArc(sketch, "E252.trimOffspring", {"start": v(328.85, 16) * mm, "mid": v(324, 27.13) * mm, "end": v(316.78, 36.9) * mm});
            skArc(sketch, "E253.trimOffspring", {"start": v(330.67, -8) * mm, "mid": v(331.26, 0) * mm, "end": v(330.67, 8) * mm});
            skArc(sketch, "E254.trimOffspring", {"start": v(316.78, -36.9) * mm, "mid": v(324, -27.13) * mm, "end": v(328.85, -16) * mm});
            skArc(sketch, "E255.trimOffspring", {"start": v(296.9, -50.48) * mm, "mid": v(304.13, -47) * mm, "end": v(310.76, -42.48) * mm});
            skArc(sketch, "E256.trimOffspring", {"start": v(264.93, -52.9) * mm, "mid": v(277, -54.26) * mm, "end": v(289.07, -52.9) * mm});
            skArc(sketch, "E257.trimOffspring", {"start": v(243.24, -42.48) * mm, "mid": v(249.87, -47) * mm, "end": v(257.1, -50.48) * mm});
            skPoint(sketch, "E258.0", {"position": v(228.9, -8) * mm});
            skSolve(sketch);
        }
        {
            var Q0;
            Q0 = qSketchRegion(id + "F40", true);
            extrude(context, id + "F41", {"entities" : qUnion([Q0]), "depth" : 8 * mm, "offsetDistance" : 25 * mm});
        }
        {
            var Q0;
            Q0=makeQuery(id+"F31.opExtrude","SWEPT_FACE",FACE,{"disambiguationData":[OSD([sQuery(id+"F30.wireOp",EDGE,"E195")])]});
            cPlane(context, id + "F42", {"entities" : qUnion([Q0]), "cplaneType" : CPlaneType.OFFSET, "offset" : 0 * mm, "width" : 150 * mm, "height" : 150 * mm});
        }
        {
            var Q0;
            Q0=qCreatedBy(id+"F42.planeOp",FACE);
            var sketch = newSketch(context, id + "F43", { "sketchPlane" : qUnion([Q0])});
            skCircle(sketch, "E259.0", {"center": v(277, 0) * mm, "radius": 22 * mm, "construction": true});
            skPoint(sketch, "E260.0", {"position": v(213.8, -8) * mm});
            skArc(sketch, "E261", {"start": v(208.26, 8) * mm, "mid": v(207.8, 0) * mm, "end": v(208.26, -8) * mm});
            skCircle(sketch, "E262", {"center": v(277, 0) * mm, "radius": 56.7 * mm});
            skLineSegment(sketch, "E263", {"start": v(264.52, 0) * mm, "end": v(197.91, 0) * mm, "construction": true});
            skLineSegment(sketch, "E264", {"start": v(208.26, 8) * mm, "end": v(214.26, 8) * mm});
            skLineSegment(sketch, "E265", {"start": v(214.26, 8) * mm, "end": v(214.26, 16) * mm});
            skLineSegment(sketch, "E266", {"start": v(214.26, 16) * mm, "end": v(209.67, 16) * mm});
            skLineSegment(sketch, "E267.MirrorCS", {"start": v(208.26, -8) * mm, "end": v(214.26, -8) * mm});
            skLineSegment(sketch, "E268.MirrorCS", {"start": v(214.26, -16) * mm, "end": v(209.67, -16) * mm});
            skLineSegment(sketch, "E269.MirrorCS", {"start": v(214.26, -8) * mm, "end": v(214.26, -16) * mm});
            skArc(sketch, "E270.trimOffspring", {"start": v(209.67, -16) * mm, "mid": v(217.07, -34.6) * mm, "end": v(229.48, -50.31) * mm});
            skLineSegment(sketch, "E271.1.0", {"start": v(231.77, -46.34) * mm, "end": v(229.48, -50.31) * mm});
            skLineSegment(sketch, "E271.1.1", {"start": v(238.7, -50.34) * mm, "end": v(231.77, -46.34) * mm});
            skLineSegment(sketch, "E271.1.2", {"start": v(235.7, -55.53) * mm, "end": v(238.7, -50.34) * mm});
            skLineSegment(sketch, "E271.1.3", {"start": v(249.56, -63.53) * mm, "end": v(252.56, -58.34) * mm});
            skLineSegment(sketch, "E271.1.4", {"start": v(252.56, -58.34) * mm, "end": v(259.49, -62.34) * mm});
            skLineSegment(sketch, "E271.1.5", {"start": v(259.49, -62.34) * mm, "end": v(257.2, -66.31) * mm});
            skLineSegment(sketch, "E271.2.0", {"start": v(294.51, -62.34) * mm, "end": v(296.8, -66.31) * mm});
            skLineSegment(sketch, "E271.2.1", {"start": v(301.44, -58.34) * mm, "end": v(294.51, -62.34) * mm});
            skLineSegment(sketch, "E271.2.2", {"start": v(304.44, -63.53) * mm, "end": v(301.44, -58.34) * mm});
            skLineSegment(sketch, "E271.2.3", {"start": v(318.3, -55.53) * mm, "end": v(315.3, -50.34) * mm});
            skLineSegment(sketch, "E271.2.4", {"start": v(315.3, -50.34) * mm, "end": v(322.23, -46.34) * mm});
            skLineSegment(sketch, "E271.2.5", {"start": v(322.23, -46.34) * mm, "end": v(324.52, -50.31) * mm});
            skLineSegment(sketch, "E271.3.0", {"start": v(339.74, -16) * mm, "end": v(344.33, -16) * mm});
            skLineSegment(sketch, "E271.3.1", {"start": v(339.74, -8) * mm, "end": v(339.74, -16) * mm});
            skLineSegment(sketch, "E271.3.2", {"start": v(345.74, -8) * mm, "end": v(339.74, -8) * mm});
            skLineSegment(sketch, "E271.3.3", {"start": v(345.74, 8) * mm, "end": v(339.74, 8) * mm});
            skLineSegment(sketch, "E271.3.4", {"start": v(339.74, 8) * mm, "end": v(339.74, 16) * mm});
            skLineSegment(sketch, "E271.3.5", {"start": v(339.74, 16) * mm, "end": v(344.33, 16) * mm});
            skLineSegment(sketch, "E271.4.0", {"start": v(322.23, 46.34) * mm, "end": v(324.52, 50.31) * mm});
            skLineSegment(sketch, "E271.4.1", {"start": v(315.3, 50.34) * mm, "end": v(322.23, 46.34) * mm});
            skLineSegment(sketch, "E271.4.2", {"start": v(318.3, 55.53) * mm, "end": v(315.3, 50.34) * mm});
            skLineSegment(sketch, "E271.4.3", {"start": v(304.44, 63.53) * mm, "end": v(301.44, 58.34) * mm});
            skLineSegment(sketch, "E271.4.4", {"start": v(301.44, 58.34) * mm, "end": v(294.51, 62.34) * mm});
            skLineSegment(sketch, "E271.4.5", {"start": v(294.51, 62.34) * mm, "end": v(296.8, 66.31) * mm});
            skLineSegment(sketch, "E271.5.0", {"start": v(259.49, 62.34) * mm, "end": v(257.2, 66.31) * mm});
            skLineSegment(sketch, "E271.5.1", {"start": v(252.56, 58.34) * mm, "end": v(259.49, 62.34) * mm});
            skLineSegment(sketch, "E271.5.2", {"start": v(249.56, 63.53) * mm, "end": v(252.56, 58.34) * mm});
            skLineSegment(sketch, "E271.5.3", {"start": v(235.7, 55.53) * mm, "end": v(238.7, 50.34) * mm});
            skLineSegment(sketch, "E271.5.4", {"start": v(238.7, 50.34) * mm, "end": v(231.77, 46.34) * mm});
            skLineSegment(sketch, "E271.5.5", {"start": v(231.77, 46.34) * mm, "end": v(229.48, 50.31) * mm});
            skArc(sketch, "E272.trimOffspring", {"start": v(235.7, -55.53) * mm, "mid": v(242.4, -59.93) * mm, "end": v(249.56, -63.53) * mm});
            skArc(sketch, "E273.trimOffspring", {"start": v(257.2, -66.31) * mm, "mid": v(277, -69.2) * mm, "end": v(296.8, -66.31) * mm});
            skArc(sketch, "E274.trimOffspring", {"start": v(304.44, -63.53) * mm, "mid": v(311.6, -59.93) * mm, "end": v(318.3, -55.53) * mm});
            skArc(sketch, "E275.trimOffspring", {"start": v(324.52, -50.31) * mm, "mid": v(336.93, -34.6) * mm, "end": v(344.33, -16) * mm});
            skArc(sketch, "E276.trimOffspring", {"start": v(345.74, -8) * mm, "mid": v(346.2, 0) * mm, "end": v(345.74, 8) * mm});
            skArc(sketch, "E277.trimOffspring", {"start": v(344.33, 16) * mm, "mid": v(336.93, 34.6) * mm, "end": v(324.52, 50.31) * mm});
            skArc(sketch, "E278.trimOffspring", {"start": v(318.3, 55.53) * mm, "mid": v(311.6, 59.93) * mm, "end": v(304.44, 63.53) * mm});
            skArc(sketch, "E279.trimOffspring", {"start": v(296.8, 66.31) * mm, "mid": v(277, 69.2) * mm, "end": v(257.2, 66.31) * mm});
            skArc(sketch, "E280.trimOffspring", {"start": v(249.56, 63.53) * mm, "mid": v(242.4, 59.93) * mm, "end": v(235.7, 55.53) * mm});
            skArc(sketch, "E281.trimOffspring", {"start": v(229.48, 50.31) * mm, "mid": v(217.07, 34.6) * mm, "end": v(209.67, 16) * mm});
            skSolve(sketch);
        }
        {
            var Q0;
            Q0 = qSketchRegion(id + "F43", true);
            extrude(context, id + "F44", {"entities" : qUnion([Q0]), "depth" : 8 * mm, "offsetDistance" : 25 * mm});
        }
        {
            var Q0;
            Q0=makeQuery(id+"F31.opExtrude","SWEPT_FACE",FACE,{"disambiguationData":[OSD([sQuery(id+"F30.wireOp",EDGE,"E198")])]});
            cPlane(context, id + "F45", {"entities" : qUnion([Q0]), "cplaneType" : CPlaneType.OFFSET, "offset" : 0 * mm, "width" : 150 * mm, "height" : 150 * mm});
        }
        {
            var Q0;
            Q0=qCreatedBy(id+"F45.planeOp",FACE);
            var sketch = newSketch(context, id + "F46", { "sketchPlane" : qUnion([Q0])});
            skCircle(sketch, "E282.0", {"center": v(277, 0) * mm, "radius": 22 * mm, "construction": true});
            skPoint(sketch, "E283.0", {"position": v(198.65, -8) * mm});
            skArc(sketch, "E284", {"start": v(193.13, 8) * mm, "mid": v(192.74, 0) * mm, "end": v(193.13, -8) * mm});
            skCircle(sketch, "E285", {"center": v(277, 0) * mm, "radius": 71.76 * mm});
            skLineSegment(sketch, "E286", {"start": v(268.35, 0) * mm, "end": v(169.01, 0) * mm, "construction": true});
            skLineSegment(sketch, "E287", {"start": v(193.13, 8) * mm, "end": v(199.13, 8) * mm});
            skLineSegment(sketch, "E288", {"start": v(199.13, 8) * mm, "end": v(199.13, 16) * mm});
            skLineSegment(sketch, "E289", {"start": v(199.13, 16) * mm, "end": v(194.28, 16) * mm});
            skLineSegment(sketch, "E290.MirrorCS", {"start": v(193.13, -8) * mm, "end": v(199.13, -8) * mm});
            skLineSegment(sketch, "E291.MirrorCS", {"start": v(199.13, -16) * mm, "end": v(194.28, -16) * mm});
            skLineSegment(sketch, "E292.MirrorCS", {"start": v(199.13, -8) * mm, "end": v(199.13, -16) * mm});
            skLineSegment(sketch, "E293.1.0", {"start": v(228.13, -68.64) * mm, "end": v(231.13, -63.44) * mm});
            skLineSegment(sketch, "E293.1.1", {"start": v(231.13, -63.44) * mm, "end": v(224.2, -59.44) * mm});
            skLineSegment(sketch, "E293.1.2", {"start": v(224.2, -59.44) * mm, "end": v(221.78, -63.64) * mm});
            skLineSegment(sketch, "E293.1.3", {"start": v(242, -76.64) * mm, "end": v(245, -71.44) * mm});
            skLineSegment(sketch, "E293.1.4", {"start": v(245, -71.44) * mm, "end": v(251.92, -75.44) * mm});
            skLineSegment(sketch, "E293.1.5", {"start": v(251.92, -75.44) * mm, "end": v(249.5, -79.64) * mm});
            skLineSegment(sketch, "E293.2.0", {"start": v(312, -76.64) * mm, "end": v(309, -71.44) * mm});
            skLineSegment(sketch, "E293.2.1", {"start": v(309, -71.44) * mm, "end": v(302.08, -75.44) * mm});
            skLineSegment(sketch, "E293.2.2", {"start": v(302.08, -75.44) * mm, "end": v(304.5, -79.64) * mm});
            skLineSegment(sketch, "E293.2.3", {"start": v(325.87, -68.64) * mm, "end": v(322.87, -63.44) * mm});
            skLineSegment(sketch, "E293.2.4", {"start": v(322.87, -63.44) * mm, "end": v(329.8, -59.44) * mm});
            skLineSegment(sketch, "E293.2.5", {"start": v(329.8, -59.44) * mm, "end": v(332.22, -63.64) * mm});
            skLineSegment(sketch, "E293.3.0", {"start": v(360.87, -8) * mm, "end": v(354.87, -8) * mm});
            skLineSegment(sketch, "E293.3.1", {"start": v(354.87, -8) * mm, "end": v(354.87, -16) * mm});
            skLineSegment(sketch, "E293.3.2", {"start": v(354.87, -16) * mm, "end": v(359.72, -16) * mm});
            skLineSegment(sketch, "E293.3.3", {"start": v(360.87, 8) * mm, "end": v(354.87, 8) * mm});
            skLineSegment(sketch, "E293.3.4", {"start": v(354.87, 8) * mm, "end": v(354.87, 16) * mm});
            skLineSegment(sketch, "E293.3.5", {"start": v(354.87, 16) * mm, "end": v(359.72, 16) * mm});
            skLineSegment(sketch, "E293.4.0", {"start": v(325.87, 68.64) * mm, "end": v(322.87, 63.44) * mm});
            skLineSegment(sketch, "E293.4.1", {"start": v(322.87, 63.44) * mm, "end": v(329.8, 59.44) * mm});
            skLineSegment(sketch, "E293.4.2", {"start": v(329.8, 59.44) * mm, "end": v(332.22, 63.64) * mm});
            skLineSegment(sketch, "E293.4.3", {"start": v(312, 76.64) * mm, "end": v(309, 71.44) * mm});
            skLineSegment(sketch, "E293.4.4", {"start": v(309, 71.44) * mm, "end": v(302.08, 75.44) * mm});
            skLineSegment(sketch, "E293.4.5", {"start": v(302.08, 75.44) * mm, "end": v(304.5, 79.64) * mm});
            skLineSegment(sketch, "E293.5.0", {"start": v(242, 76.64) * mm, "end": v(245, 71.44) * mm});
            skLineSegment(sketch, "E293.5.1", {"start": v(245, 71.44) * mm, "end": v(251.92, 75.44) * mm});
            skLineSegment(sketch, "E293.5.2", {"start": v(251.92, 75.44) * mm, "end": v(249.5, 79.64) * mm});
            skLineSegment(sketch, "E293.5.3", {"start": v(228.13, 68.64) * mm, "end": v(231.13, 63.44) * mm});
            skLineSegment(sketch, "E293.5.4", {"start": v(231.13, 63.44) * mm, "end": v(224.2, 59.44) * mm});
            skLineSegment(sketch, "E293.5.5", {"start": v(224.2, 59.44) * mm, "end": v(221.78, 63.64) * mm});
            skArc(sketch, "E294.trimOffspring", {"start": v(194.28, -16) * mm, "mid": v(204.03, -42.13) * mm, "end": v(221.78, -63.64) * mm});
            skArc(sketch, "E295.trimOffspring", {"start": v(221.78, 63.64) * mm, "mid": v(204.03, 42.13) * mm, "end": v(194.28, 16) * mm});
            skArc(sketch, "E296.trimOffspring", {"start": v(242, 76.64) * mm, "mid": v(234.87, 72.97) * mm, "end": v(228.13, 68.64) * mm});
            skArc(sketch, "E297.trimOffspring", {"start": v(304.5, 79.64) * mm, "mid": v(277, 84.26) * mm, "end": v(249.5, 79.64) * mm});
            skArc(sketch, "E298.trimOffspring", {"start": v(325.87, 68.64) * mm, "mid": v(319.13, 72.97) * mm, "end": v(312, 76.64) * mm});
            skArc(sketch, "E299.trimOffspring", {"start": v(359.72, 16) * mm, "mid": v(349.97, 42.13) * mm, "end": v(332.22, 63.64) * mm});
            skArc(sketch, "E300.trimOffspring", {"start": v(360.87, -8) * mm, "mid": v(361.26, 0) * mm, "end": v(360.87, 8) * mm});
            skArc(sketch, "E301.trimOffspring", {"start": v(332.22, -63.64) * mm, "mid": v(349.97, -42.13) * mm, "end": v(359.72, -16) * mm});
            skArc(sketch, "E302.trimOffspring", {"start": v(312, -76.64) * mm, "mid": v(319.13, -72.97) * mm, "end": v(325.87, -68.64) * mm});
            skArc(sketch, "E303.trimOffspring", {"start": v(249.5, -79.64) * mm, "mid": v(277, -84.26) * mm, "end": v(304.5, -79.64) * mm});
            skArc(sketch, "E304.trimOffspring", {"start": v(228.13, -68.64) * mm, "mid": v(234.87, -72.97) * mm, "end": v(242, -76.64) * mm});
            skSolve(sketch);
        }
        {
            var Q0;
            Q0 = qSketchRegion(id + "F46", true);
            extrude(context, id + "F47", {"entities" : qUnion([Q0]), "depth" : 8 * mm, "offsetDistance" : 25 * mm});
        }
    });
